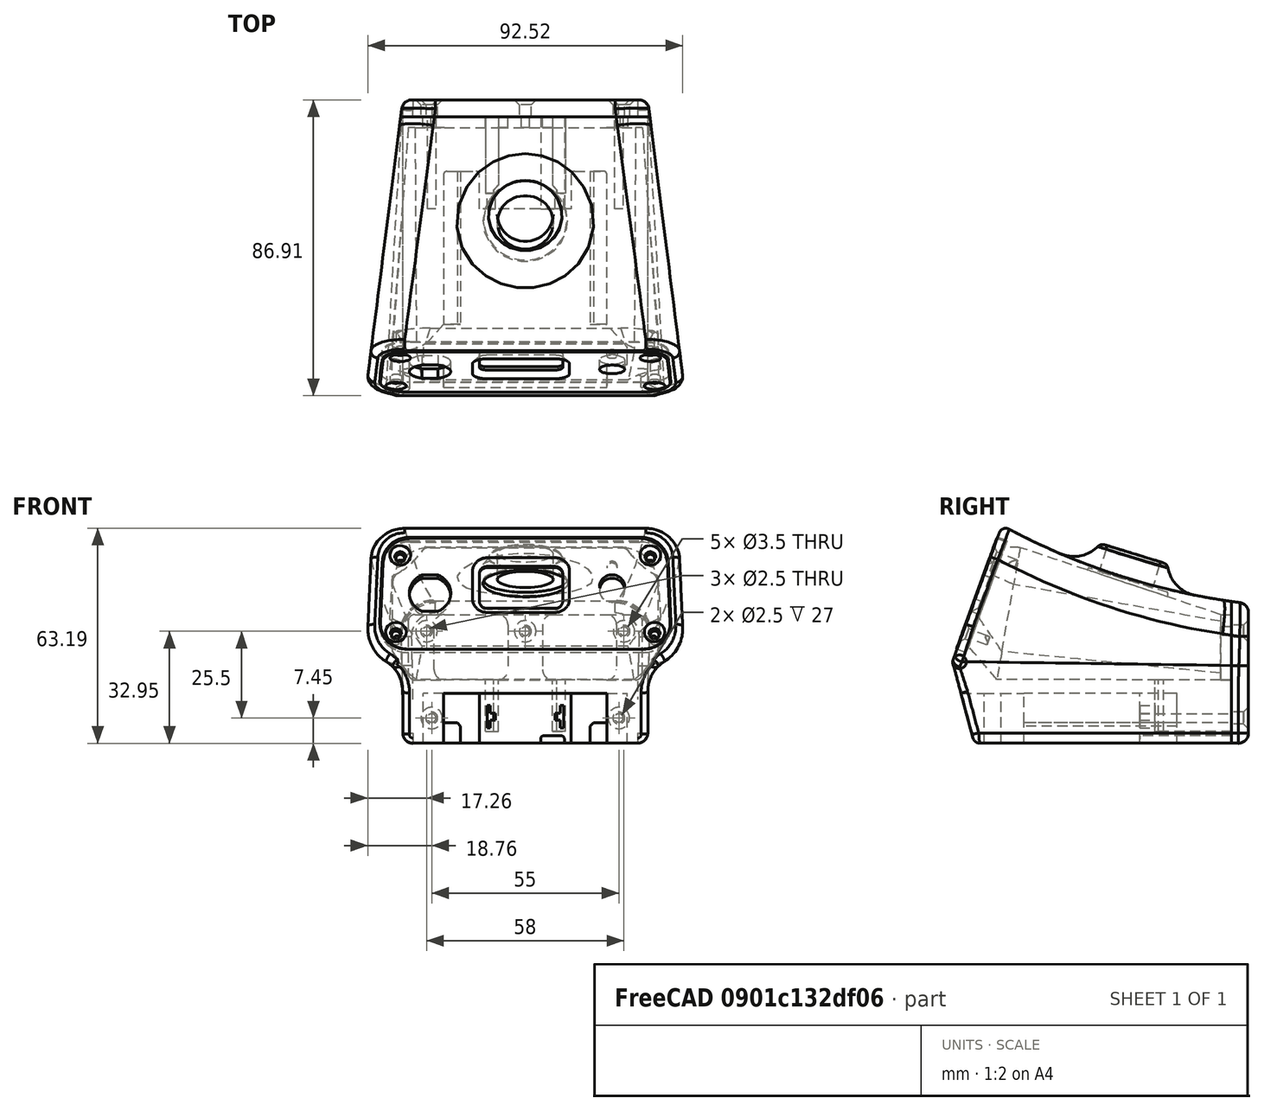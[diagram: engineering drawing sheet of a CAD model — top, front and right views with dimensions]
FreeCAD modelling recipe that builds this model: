
FCSTD DOCUMENT  (FreeCAD 2022.709R28846 (Git))
Label: solder_station4b_snap
License: All rights reserved
LicenseURL: http://en.wikipedia.org/wiki/All_rights_reserved
objects: Sketcher::SketchObject×20, PartDesign::Pocket×10, PartDesign::Fillet×8, Mesh::Feature×4, Part::FeaturePython×3, App::DocumentObjectGroup×3, PartDesign::Chamfer×3, PartDesign::Body×3, PartDesign::FeatureBase×2, PartDesign::Pad×2, Spreadsheet::Sheet×1, Part::Plane×1, Part::Loft×1, Part::Extrusion×1, Part::MultiCommon×1, PartDesign::SubtractiveLoft×1, PartDesign::Revolution×1, PartDesign::Groove×1, App::Part×1
note: 112 computed .brp shape members not serialized (recipe doc carries the construction recipe); baked Part::Feature solids carry a one-line shape summary decoded from their .brp

FEATURE [Sketcher::SketchObject] Sketch  label="RearSupport"
  ArcFitTolerance = 0
  AttachmentOffset = pos=(0,0,-37.8) rot=(0,0,1;0rad)
  AttachmentSupport = -> [XZ_Plane005]
  FullyConstrained = true
  MapMode = 5
  Placement = pos=(0,37.8,8.4e-15) rot=(1,0,0;1.5708rad)
  Support = -> [XZ_Plane005]
  TreeRank = 0
  expr: AttachmentOffset.Base.z = -<<param>>.mid_depth / 2 + <<param>>.wall
  expr: Constraints[24] = 3
  expr: Constraints[37] = <<param>>.bottom_height
  expr: Constraints[38] = <<param>>.floor
  expr: Constraints[39] = <<param>>.rear_height - <<param>>.wall
  expr: Constraints[47] = <<param>>.reart_screw_width2
  expr: Constraints[48] = <<param>>.rear_screw_width1
  expr: Constraints[49] = <<param>>.screw_hole
  expr: Constraints[50] = <<param>>.rear_screw_height
  expr: Constraints[51] = <<param>>.rear_screw_height
  expr: Constraints[52] = <<param>>.rear_screw_offset
  sketch-geometry (22):
    g0: LineSegment StartX=-23.8 StartY=13.8 StartZ=0 EndX=-8.1 EndY=13.8 EndZ=0
    g1: LineSegment StartX=26.8 StartY=10.8 StartZ=0 EndX=26.8 EndY=-2.4 EndZ=0
    g2: LineSegment StartX=23.8 StartY=-5.4 StartZ=0 EndX=8.1 EndY=-5.4 EndZ=0
    g3: LineSegment StartX=-26.8 StartY=-2.4 StartZ=0 EndX=-26.8 EndY=10.8 EndZ=0
    g4: LineSegment StartX=-5.1 StartY=10.8 StartZ=0 EndX=-5.1 EndY=-2.4 EndZ=0
    g5: LineSegment StartX=5.1 StartY=10.8 StartZ=0 EndX=5.1 EndY=-2.4 EndZ=0
    g6: LineSegment StartX=8.1 StartY=13.8 StartZ=0 EndX=23.8 EndY=13.8 EndZ=0
    g7: LineSegment StartX=-8.1 StartY=-5.4 StartZ=0 EndX=-23.8 EndY=-5.4 EndZ=0
    g8: ArcOfCircle CenterX=-8.1 CenterY=10.8 CenterZ=0 NormalX=0 NormalY=0 NormalZ=1 AngleXU=0 Radius=3 StartAngle=0 EndAngle=1.5708
    g9: ArcOfCircle CenterX=8.1 CenterY=10.8 CenterZ=0 NormalX=0 NormalY=0 NormalZ=1 AngleXU=0 Radius=3 StartAngle=1.5708 EndAngle=3.14159
    g10: ArcOfCircle CenterX=-8.1 CenterY=-2.4 CenterZ=0 NormalX=0 NormalY=0 NormalZ=1 AngleXU=0 Radius=3 StartAngle=4.71239 EndAngle=6.28319
    g11: ArcOfCircle CenterX=8.1 CenterY=-2.4 CenterZ=0 NormalX=0 NormalY=0 NormalZ=1 AngleXU=0 Radius=3 StartAngle=3.14159 EndAngle=4.71239
    g12: ArcOfCircle CenterX=-23.8 CenterY=10.8 CenterZ=0 NormalX=0 NormalY=0 NormalZ=1 AngleXU=0 Radius=3 StartAngle=1.5708 EndAngle=3.14159
    g13: ArcOfCircle CenterX=-23.8 CenterY=-2.4 CenterZ=0 NormalX=0 NormalY=0 NormalZ=1 AngleXU=0 Radius=3 StartAngle=3.14159 EndAngle=4.71239
    g14: ArcOfCircle CenterX=23.8 CenterY=10.8 CenterZ=0 NormalX=0 NormalY=0 NormalZ=1 AngleXU=0 Radius=3 StartAngle=0 EndAngle=1.5708
    g15: ArcOfCircle CenterX=23.8 CenterY=-2.4 CenterZ=0 NormalX=0 NormalY=0 NormalZ=1 AngleXU=0 Radius=3 StartAngle=4.71239 EndAngle=6.28319
    g16: Circle [constr] CenterX=0 CenterY=-24 CenterZ=0 NormalX=0 NormalY=0 NormalZ=1 AngleXU=0 Radius=3
    g17: Circle CenterX=0 CenterY=8.9 CenterZ=0 NormalX=0 NormalY=0 NormalZ=1 AngleXU=0 Radius=1.25
    g18: Circle CenterX=-29 CenterY=8.9 CenterZ=0 NormalX=0 NormalY=0 NormalZ=1 AngleXU=0 Radius=1.25
    g19: Circle [constr] CenterX=-27.5 CenterY=-16.6 CenterZ=0 NormalX=0 NormalY=0 NormalZ=1 AngleXU=0 Radius=1.25
    g20: Circle [constr] CenterX=27.5 CenterY=-16.6 CenterZ=0 NormalX=0 NormalY=0 NormalZ=1 AngleXU=0 Radius=1.25
    g21: Circle CenterX=29 CenterY=8.9 CenterZ=0 NormalX=0 NormalY=0 NormalZ=1 AngleXU=0 Radius=1.25
  constraints (53):
    c: Horizontal(g0)
    c: Horizontal(g2)
    c: Vertical(g1)
    c: Vertical(g3)
    c: Vertical(g4)
    c: Vertical(g5)
    c: Tangent(g0,g6)
    c: Tangent(g2,g7)
    c: Tangent(g0,g8) = 1.5708
    c: Tangent(g4,g8) = 1.5708
    c: Tangent(g5,g9) = -1.5708
    c: Tangent(g6,g9) = 1.5708
    c: Tangent(g7,g10) = 1.5708
    c: Tangent(g4,g10) = 1.5708
    c: Tangent(g5,g11) = -1.5708
    c: Tangent(g2,g11) = 1.5708
    c: Tangent(g0,g12) = 1.5708
    c: Tangent(g3,g12) = 1.5708
    c: Tangent(g3,g13) = 1.5708
    c: Tangent(g7,g13) = 1.5708
    c: Tangent(g6,g14) = 1.5708
    c: Tangent(g1,g14) = 1.5708
    c: Tangent(g1,g15) = 1.5708
    c: Tangent(g2,g15) = 1.5708
    c: Radius(g9) = 3
    c: Equal(g12,g13)
    c: Equal(g13,g10)
    c: Equal(g10,g8)
    c: Equal(g11,g15)
    c: Equal(g15,g14)
    c: Equal(g14,g9)
    c: DistanceX(g4,g-1) = 5.1
    c: DistanceX(g5,g1) = 21.7
    c: Symmetric(g4,g5,g-2)
    c: Equal(g7,g2)
    c: PointOnObject(g16,g-2)
    c: Radius(g16) = 3
    c: DistanceY(g16,g-1) = 24
    c: DistanceY(g16,g2) = 18.6
    c: DistanceY(g16,g6) = 37.8
    c: PointOnObject(g17,g-2)
    c: Equal(g21,g18)
    c: Equal(g18,g19)
    c: Equal(g19,g20)
    c: Equal(g18,g17)
    c: Symmetric(g20,g19,g-2)
    c: Symmetric(g18,g21,g-2)
    c: DistanceX(g19,g20) = 55
    c: DistanceX(g18,g21) = 58
    c: Diameter(g19) = 2.5
    c: DistanceY(g20,g21) = 25.5
    c: DistanceY(g20,g17) = 25.5
    c: DistanceY(g16,g19) = 7.4
FEATURE [Spreadsheet::Sheet] Spreadsheet  label="param"
  PythonMode = false
  ShowCells = 0
  TreeRank = 0
  cells = A1=Body; B2=top_depth; C2(top_depth)=70; B3=mid_depth; C3(mid_depth)=82; D3=Half value is the rear reference point; B4=bottom_depth; C4(bottom_depth)=75; B6=bottom_width; C6(bottom_width)=72; B7=bottom_height; C7(bottom_height)=24; B8=bottom_angle; C8(bottom_angle)=15; B10=rear_width; C10(rear_width)=72; B11=rear_height; C11(rear_height)=41; B13=mid_width; C13(mid_width)=80; B14=mid_height; C14(mid_height)=52; D14=was 50; B16=front_width1; C16(front_width1)=91; D16=@top (upper); B17=front_width2; C17(front_width2)=94; D17=@mid (lower); B18=front_height; C18(front_height)=64; B19=front_angle; C19(front_angle)=20; D19=20 is actual value; B21=wall; C21(wall)=3.2; B22=radius_big; C22(radius_big)=10; B23=radius_medium; C23(radius_medium)=3; B24=radius_small; C24(radius_small)=2; B25=arch; C25(arch)=200; A27=Button; B28=button_offset; C28(button_offset)=10; B29=button_inside_dia; C29(button_inside_dia)=20; B30=button_outside_dia; C30(button_outside_dia)=22; B31=button_height; C31(button_height)=24; B32=button_extension; C32(button_extension)=8; B33=button_fillet; C33(button_fillet)=12; B34=button_angle; C34(button_angle)=-17; B35=button_hole; C35(button_hole)=16.4; B36=button_hole_center; C36(button_hole_center)=-0.5; A38=Battery Cuts; B39=batt_carveout; C39(batt_carveout)=14.6; B40=batt_rail; C40(batt_rail)=6; B41=batt_rail_length; C41(batt_rail_length)=45; A43=Terminal Pockets; B44=terminal_height; C44(terminal_height)=6.6; B45=terminal_thickness; C45(terminal_thickness)=1; B46=terminal_seperation; C46(terminal_seperation)=21.5; B47=terminal_offset; C47(terminal_offset)=4.5; B48=terminal_depth; C48(terminal_depth)=22.5; A50=Box Interior; B51=floor; C51(floor)=18.6; B52=rear_inside_width; C52(rear_inside_width)==C10 - C21; D52=Calculated; B53=rear_inside_height; C53(rear_inside_height)==C11 - C21; D53=Calculated; B54=mid_inside_width; C54(mid_inside_width)==C13; D54=Calculated; B55=mid_inside_height; C55(mid_inside_height)==C14 + 6; D55=Calculated; B56=front_inside_width1; C56(front_inside_width1)==C63 - C59 * 2; D56=Calculated (upper); B57=front_inside_width2; C57(front_inside_width2)==C64 - C59 * 2; D57=Calculated (lower); B58=front_inside_height; C58(front_inside_height)==C65 - C60 * 2; D58=Calculated; B59=front_width_lip_width; C59(front_width_lip_width)=3; B60=front_inside_lip_height; C60(front_inside_lip_height)=2; A62=Face; B63=face_width1; C63(face_width1)=84; D63=Dimension of opening in case (upper); B64=face_width2; C64(face_width2)=85.5; D64=Dimension of opening in case (lower); B65=face_height; C65(face_height)==34 + 1; D65=Dimension of actual opening in case; B66=face_fit; C66(face_fit)=0.4; D66=Reduction of face dimensions for clearance with case; B67=face_thickness; C67(face_thickness)=3; D67=Face thickness; B68=face_radius; C68(face_radius)=8; D68=Corner radius; B69=face_offset; C69(face_offset)=2.8; D69=Axis origin to bottom face (reference); B70=face_knob_x; C70(face_knob_x)=25.5; D70=Vertical center line of face to center of knob; B71=face_knob_y; C71(face_knob_y)=19.5; D71=Bottom of face to center of knob; E71=was 20.5; B72=face_knob_tab; C72(face_knob_tab)=7; D72=Center to center distance of rotary dial shaft to tab; B73=face_knob_hole; C73(face_knob_hole)=7.4; D73=Hole size fo shaft; B74=face_screen_x; C74(face_screen_x)=14.5; D74=Center of knob to right edge of screen; B75=face_screen_y; C75(face_screen_y)=20; D75=Bottom of face to center of screen; E75=was 21; B76=face_screen_width; C76(face_screen_width)=24.5; D76=Width of screen opening; B77=face_screen_height; C77(face_screen_height)=13.1; D77=Height of screen opening; B78=face_screen_radius; C78(face_screen_radius)=2.25; D78=Radius of screen opening; B79=face_plug_x; C79(face_plug_x)=28; D79=Center line of face to center of plug; B80=face_plug_y; C80(face_plug_y)=17.5; D80=Bottom of face to center of plug; B81=face_plug_hole; C81(face_plug_hole)=12.2; D81=Hole size for plug body; A83=Screws; B84=screw_hole; C84(screw_hole)=2.5; D84=Screw hole diameter; B86=front_screw_width1; C86(front_screw_width1)=73.5; D86=Screw center to center distance (upper); B87=front_screw_width2; C87(front_screw_width2)=76; D87=Screw center to center distance (lower); B88=front_screw_height; C88(front_screw_height)=24; D88=Screw center to center distance (top to bottom); B89=front_screw_offset; C89(front_screw_offset)=5.5; D89=Bottom of face to center of screws (lower); B91=rear_screw_width1; C91(rear_screw_width1)=58; D91=Screw center to center distance (upper); B92=reart_screw_width2; C92(reart_screw_width2)=55; D92=Screw center to center distance (lower); B93=rear_screw_height; C93(rear_screw_height)=25.5; D93=Screw center to center distance (top to bottom); B94=rear_screw_offset; C94(rear_screw_offset)=7.4; A96=Back; B97=back_thickness; C97(back_thickness)=5
FEATURE [Sketcher::SketchObject] Sketch008  label="SketchButtonHole"
  ArcFitTolerance = 0
  AttachmentOffset = pos=(0,-0.5,24) rot=(1,0,0;-0.296706rad)
  AttachmentSupport = -> [XY_Plane005]
  FullyConstrained = true
  MapMode = 5
  Placement = pos=(0,-0.5,24) rot=(1,0,0;5.98648rad)
  Support = -> [XY_Plane005]
  TreeRank = 0
  expr: AttachmentOffset.Base.y = <<param>>.button_hole_center
  expr: AttachmentOffset.Base.z = <<param>>.button_height
  expr: AttachmentOffset.Rotation.Angle = <<param>>.button_angle
  expr: Constraints[0] = <<param>>.button_hole
  expr: Constraints[2] = <<param>>.button_offset
  sketch-geometry (1):
    g0: Circle CenterX=0 CenterY=10 CenterZ=0 NormalX=0 NormalY=0 NormalZ=1 AngleXU=0 Radius=8.2
  constraints (3):
    c: Diameter(g0) = 16.4
    c: PointOnObject(g0,g-2)
    c: DistanceY(g-1,g0) = 10
FEATURE [Sketcher::SketchObject] Sketch012  label="SketchSide"
  ArcFitTolerance = 0
  AttachmentOffset = pos=(2.5,0,0) rot=(0,0,1;0rad)
  AttachmentSupport = -> [YZ_Plane006]
  FullyConstrained = true
  MapMode = 5
  Placement = pos=(6e-16,2.5,-6e-16) rot=(0.57735,0.57735,0.57735;2.0944rad)
  Support = -> [YZ_Plane006]
  TreeRank = 0
  expr: AttachmentOffset.Base.x = <<param>>.back_thickness / 2
  expr: Constraints[10] = <<param>>.bottom_height
  expr: Constraints[11] = 90 - <<param>>.bottom_angle
  expr: Constraints[12] = 90 - <<param>>.front_angle
  expr: Constraints[16] = <<param>>.front_height
  expr: Constraints[4] = <<param>>.rear_height - <<param>>.bottom_height
  expr: Constraints[5] = <<param>>.arch
  expr: Constraints[6] = <<param>>.mid_depth + <<param>>.back_thickness
  sketch-geometry (6):
    g0: LineSegment StartX=43.5 StartY=0 StartZ=0 EndX=43.5 EndY=17 EndZ=0
    g1: LineSegment StartX=-43.5 StartY=0 StartZ=0 EndX=-28.9412 EndY=40 EndZ=0
    g2: ArcOfCircle CenterX=66.6993 CenterY=215.65 CenterZ=0 NormalX=0 NormalY=0 NormalZ=1 AngleXU=0 Radius=200 StartAngle=4.21378 EndAngle=4.59613
    g3: LineSegment StartX=-43.5 StartY=0 StartZ=0 EndX=-37.0692 EndY=-24 EndZ=0
    g4: LineSegment StartX=-37.0692 StartY=-24 StartZ=0 EndX=43.5 EndY=-24 EndZ=0
    g5: LineSegment StartX=43.5 StartY=-24 StartZ=0 EndX=43.5 EndY=0 EndZ=0
  constraints (18):
    c: PointOnObject(g1,g-1)
    c: Vertical(g0)
    c: Coincident(g2,g0)
    c: Symmetric(g1,g0,g-2)
    c: DistanceY(g0,g0) = 17
    c: Radius(g2) = 200
    c: DistanceX(g1,g0) = 87
    c: Horizontal(g4)
    c: Coincident(g5,g4)
    c: Vertical(g5)
    c: DistanceY(g4,g-1) = 24
    c: Angle(g3,g-1) = 1.309
    c: Angle(g-1,g1) = 1.22173
    c: Coincident(g3,g1)
    c: Coincident(g5,g0)
    c: Coincident(g2,g1)
    c: DistanceY(g4,g1) = 64
    c: Coincident(g4,g3)
FEATURE [Sketcher::SketchObject] Sketch018  label="SketchBat1"
  ArcFitTolerance = 0
  AttachmentOffset = pos=(0,0,-24) rot=(0,0,1;0rad)
  AttachmentSupport = -> [XY_Plane005]
  FullyConstrained = true
  MapMode = 5
  Placement = pos=(0,0,-24) rot=(0,0,1;0rad)
  Support = -> [XY_Plane005]
  TreeRank = 0
  expr: AttachmentOffset.Base.z = -<<param>>.bottom_height
  expr: Constraints[63] = <<param>>.batt_rail_length
  expr: Constraints[64] = <<param>>.mid_depth / 2
  sketch-geometry (21):
    g0: LineSegment StartX=-24 StartY=-41.7082 StartZ=0 EndX=24 EndY=-41.7082 EndZ=0
    g1: LineSegment StartX=24 StartY=-41.7082 StartZ=0 EndX=24 EndY=-31.7082 EndZ=0
    g2: LineSegment StartX=24 StartY=-31.7082 StartZ=0 EndX=30 EndY=-31.7082 EndZ=0
    g3: LineSegment StartX=30 StartY=-31.7082 StartZ=0 EndX=30 EndY=-26.7082 EndZ=0
    g4: LineSegment StartX=30 StartY=-26.7082 StartZ=0 EndX=24 EndY=-20 EndZ=0
    g5: LineSegment StartX=24 StartY=-20 StartZ=0 EndX=24 EndY=24 EndZ=0
    g6: LineSegment StartX=13.5 StartY=24 StartZ=0 EndX=13.5 EndY=14 EndZ=0
    g7: LineSegment StartX=13.5 StartY=14 StartZ=0 EndX=-13.5 EndY=14 EndZ=0
    g8: LineSegment StartX=-13.5 StartY=14 StartZ=0 EndX=-13.5 EndY=24 EndZ=0
    g9: LineSegment StartX=-24 StartY=24 StartZ=0 EndX=-24 EndY=-20 EndZ=0
    g10: LineSegment StartX=-24 StartY=-20 StartZ=0 EndX=-30 EndY=-26.7082 EndZ=0
    g11: LineSegment StartX=-30 StartY=-26.7082 StartZ=0 EndX=-30 EndY=-31.7082 EndZ=0
    g12: LineSegment StartX=-30 StartY=-31.7082 StartZ=0 EndX=-24 EndY=-31.7082 EndZ=0
    g13: LineSegment StartX=-24 StartY=-31.7082 StartZ=0 EndX=-24 EndY=-41.7082 EndZ=0
    g14: Circle [constr] CenterX=0 CenterY=41 CenterZ=0 NormalX=0 NormalY=0 NormalZ=1 AngleXU=0 Radius=4
    g15: ArcOfCircle CenterX=-14.5 CenterY=24 CenterZ=0 NormalX=0 NormalY=0 NormalZ=1 AngleXU=0 Radius=1 StartAngle=6.28318 EndAngle=7.85399
    g16: LineSegment StartX=-23 StartY=25 StartZ=0 EndX=-14.5 EndY=25 EndZ=0
    g17: LineSegment StartX=14.5 StartY=25 StartZ=0 EndX=23 EndY=25 EndZ=0
    g18: ArcOfCircle CenterX=-23 CenterY=24 CenterZ=0 NormalX=0 NormalY=0 NormalZ=1 AngleXU=0 Radius=1 StartAngle=1.57079 EndAngle=3.1416
    g19: ArcOfCircle CenterX=14.5 CenterY=24 CenterZ=0 NormalX=0 NormalY=0 NormalZ=1 AngleXU=0 Radius=1 StartAngle=1.5708 EndAngle=3.14159
    g20: ArcOfCircle CenterX=23 CenterY=24 CenterZ=0 NormalX=0 NormalY=0 NormalZ=1 AngleXU=0 Radius=1.00001 StartAngle=2.75124e-06 EndAngle=1.5708
  constraints (65):
    c: Horizontal(g0)
    c: Coincident(g1,g0)
    c: Vertical(g1)
    c: Coincident(g2,g1)
    c: Horizontal(g2)
    c: Coincident(g3,g2)
    c: Coincident(g3,g4)
    c: Vertical(g5)
    c: Coincident(g6,g7)
    c: Coincident(g7,g8)
    c: Vertical(g8)
    c: Vertical(g9)
    c: Coincident(g10,g11)
    c: Vertical(g11)
    c: Coincident(g11,g12)
    c: Horizontal(g12)
    c: Coincident(g12,g13)
    c: Equal(g6,g8)
    c: Equal(g5,g9)
    c: Equal(g4,g10)
    c: Equal(g3,g11)
    c: Equal(g12,g2)
    c: Equal(g1,g13)
    c: Coincident(g13,g0)
    c: Vertical(g13)
    c: DistanceX(g7,g7) = 27
    c: Symmetric(g7,g6,g-2)
    c: Distance(g4) = 9
    c: Vertical(g3)
    c: DistanceY(g3,g3) = 5
    c: DistanceX(g2,g2) = 6
    c: DistanceY(g1,g1) = 10
    c: DistanceX(g0,g0) = 48
    c: PointOnObject(g14,g-2)
    c: Coincident(g9,g10)
    c: Coincident(g5,g4)
    c: Coincident(g15,g8)
    c: Coincident(g16,g15)
    c: Tangent(g15,g8)
    c: Horizontal(g16)
    c: Horizontal(g17)
    c: DistanceX(g9,g5) = 48
    c: Symmetric(g4,g9,g-2)
    c: Equal(g16,g17)
    c: Coincident(g18,g9)
    c: Coincident(g18,g16)
    c: Equal(g18,g15)
    c: Tangent(g18,g16)
    c: Tangent(g18,g9)
    c: DistanceY(g6,g17) = 11
    c: Vertical(g6)
    c: Coincident(g19,g6)
    c: Coincident(g19,g17)
    c: Coincident(g20,g17)
    c: Coincident(g20,g5)
    c: Tangent(g20,g17)
    c: Tangent(g20,g5)
    c: Tangent(g19,g6)
    c: Tangent(g19,g17)
    c: Equal(g15,g19)
    c: Radius(g19) = 1
    c: Radius(g14) = 4
    c: DistanceY(g15,g14) = 16
    c: DistanceY(g9,g16) = 45
    c: DistanceY(g-1,g14) = 41
FEATURE [Sketcher::SketchObject] Sketch019  label="SketchBat2"
  ArcFitTolerance = 0
  AttachmentOffset = pos=(0,0,-25) rot=(0,0,1;0rad)
  AttachmentSupport = -> [XZ_Plane005]
  FullyConstrained = true
  MapMode = 5
  Placement = pos=(0,25,5.6e-15) rot=(1,0,0;1.5708rad)
  Support = -> [XZ_Plane005]
  TreeRank = 0
  expr: AttachmentOffset.Base.z = -<<param>>.mid_depth / 2 + 16
  expr: Constraints[17] = <<param>>.bottom_height
  expr: Constraints[18] = <<param>>.batt_rail
  expr: Constraints[19] = 48.01mm
  sketch-geometry (10):
    g0: LineSegment StartX=-24.005 StartY=-18 StartZ=0 EndX=-20.005 EndY=-18 EndZ=0
    g1: LineSegment StartX=-19.005 StartY=-24 StartZ=0 EndX=-24.005 EndY=-24 EndZ=0
    g2: LineSegment StartX=-24.005 StartY=-24 StartZ=0 EndX=-24.005 EndY=-18 EndZ=0
    g3: LineSegment StartX=24.005 StartY=-18 StartZ=0 EndX=20.005 EndY=-18 EndZ=0
    g4: LineSegment StartX=19.005 StartY=-24 StartZ=0 EndX=24.005 EndY=-24 EndZ=0
    g5: LineSegment StartX=24.005 StartY=-24 StartZ=0 EndX=24.005 EndY=-18 EndZ=0
    g6: LineSegment StartX=-19.005 StartY=-19 StartZ=0 EndX=-19.005 EndY=-24 EndZ=0
    g7: LineSegment StartX=19.005 StartY=-24 StartZ=0 EndX=19.005 EndY=-19 EndZ=0
    g8: LineSegment StartX=-20.005 StartY=-18 StartZ=0 EndX=-19.005 EndY=-19 EndZ=0
    g9: LineSegment StartX=19.005 StartY=-19 StartZ=0 EndX=20.005 EndY=-18 EndZ=0
  constraints (29):
    c: Coincident(g1,g2)
    c: Coincident(g2,g0)
    c: Horizontal(g0)
    c: Horizontal(g1)
    c: Vertical(g2)
    c: Coincident(g4,g5)
    c: Coincident(g5,g3)
    c: Horizontal(g3)
    c: Horizontal(g4)
    c: Vertical(g5)
    c: Coincident(g6,g1)
    c: Vertical(g6)
    c: Equal(g1,g4)
    c: Coincident(g7,g4)
    c: Vertical(g7)
    c: Equal(g6,g7)
    c: Symmetric(g1,g4,g-2)
    c: DistanceY(g1,g-1) = 24
    c: DistanceY(g4,g3) = 6
    c: DistanceX(g1,g4) = 48.01
    c: DistanceX(g4,g4) = 5
    c: Coincident(g8,g0)
    c: Coincident(g8,g6)
    c: Coincident(g9,g7)
    c: Coincident(g9,g3)
    c: Equal(g0,g3)
    c: Equal(g2,g5)
    c: DistanceX(g0,g0) = 4
    c: DistanceY(g1,g6) = 5
FEATURE [Sketcher::SketchObject] Sketch021  label="SketchButton"
  ArcFitTolerance = 0
  AttachmentOffset = pos=(10,24,0) rot=(0,0,1;-0.296706rad)
  AttachmentSupport = -> [YZ_Plane005]
  FullyConstrained = true
  MapMode = 5
  Placement = pos=(-3.1e-15,10,24) rot=(-0.51122,-0.690875,-0.51122;4.35074rad)
  Support = -> [YZ_Plane005]
  TreeRank = 0
  expr: AttachmentOffset.Base.x = <<param>>.button_offset
  expr: AttachmentOffset.Base.y = <<param>>.button_height
  expr: AttachmentOffset.Rotation.Angle = <<param>>.button_angle
  expr: Constraints[6] = <<param>>.button_extension
  expr: Constraints[7] = <<param>>.button_outside_dia / 2
  sketch-geometry (5):
    g0: LineSegment StartX=0 StartY=0 StartZ=0 EndX=0 EndY=8 EndZ=0
    g1: LineSegment StartX=0 StartY=8 StartZ=0 EndX=9 EndY=8 EndZ=0
    g2: LineSegment StartX=0 StartY=0 StartZ=0 EndX=11 EndY=0 EndZ=0
    g3: LineSegment StartX=11 StartY=0 StartZ=0 EndX=11 EndY=6 EndZ=0
    g4: ArcOfCircle CenterX=9 CenterY=6 CenterZ=0 NormalX=0 NormalY=0 NormalZ=1 AngleXU=0 Radius=2 StartAngle=1.123e-13 EndAngle=1.5708
  constraints (13):
    c: Coincident(g0,g-1)
    c: PointOnObject(g0,g-2)
    c: Coincident(g1,g0)
    c: Horizontal(g1)
    c: Coincident(g2,g0)
    c: Horizontal(g2)
    c: DistanceY(g0,g0) = 8
    c: DistanceX(g2,g2) = 11
    c: Coincident(g3,g2)
    c: Vertical(g3)
    c: Radius(g4) = 2
    c: Tangent(g4,g3) = -1.5708
    c: Tangent(g4,g1) = 1.5708
FEATURE [Sketcher::SketchObject] Sketch022  label="SketchRearInside"
  ArcFitTolerance = 0
  AttachmentOffset = pos=(0,0,-37.8) rot=(0,0,1;0rad)
  AttachmentSupport = -> [XZ_Plane005]
  FullyConstrained = true
  MapMode = 5
  Placement = pos=(0,37.8,8.4e-15) rot=(1,0,0;1.5708rad)
  Support = -> [XZ_Plane005]
  TreeRank = 0
  expr: AttachmentOffset.Base.z = -<<param>>.mid_depth / 2 + <<param>>.wall
  expr: Constraints[12] = <<param>>.radius_small
  expr: Constraints[18] = <<param>>.rear_inside_width
  expr: Constraints[26] = <<param>>.bottom_height
  expr: Constraints[27] = <<param>>.rear_inside_height
  expr: Constraints[29] = <<param>>.floor
  sketch-geometry (9):
    g0: LineSegment StartX=-34.4 StartY=11.8 StartZ=0 EndX=-34.4 EndY=-3.39998 EndZ=0
    g1: LineSegment StartX=-32.4 StartY=-5.4 StartZ=0 EndX=32.4 EndY=-5.4 EndZ=0
    g2: LineSegment StartX=34.4 StartY=-3.39998 StartZ=0 EndX=34.4 EndY=11.8 EndZ=0
    g3: LineSegment StartX=-32.4 StartY=13.8 StartZ=0 EndX=32.4 EndY=13.8 EndZ=0
    g4: ArcOfCircle CenterX=32.4 CenterY=11.8 CenterZ=0 NormalX=0 NormalY=0 NormalZ=1 AngleXU=0 Radius=2 StartAngle=6.28318 EndAngle=7.85399
    g5: ArcOfCircle CenterX=32.4 CenterY=-3.4 CenterZ=0 NormalX=0 NormalY=0 NormalZ=1 AngleXU=0 Radius=2 StartAngle=4.71238 EndAngle=6.28319
    g6: ArcOfCircle CenterX=-32.4 CenterY=11.8 CenterZ=0 NormalX=0 NormalY=0 NormalZ=1 AngleXU=0 Radius=2 StartAngle=1.57079 EndAngle=3.1416
    g7: ArcOfCircle CenterX=-32.4 CenterY=-3.4 CenterZ=0 NormalX=0 NormalY=0 NormalZ=1 AngleXU=0 Radius=2 StartAngle=3.14158 EndAngle=4.71239
    g8: Circle [constr] CenterX=0 CenterY=-24 CenterZ=0 NormalX=0 NormalY=0 NormalZ=1 AngleXU=0 Radius=3
  constraints (30):
    c: Vertical(g0)
    c: Horizontal(g1)
    c: Vertical(g2)
    c: Horizontal(g3)
    c: Equal(g3,g1)
    c: Equal(g0,g2)
    c: Coincident(g4,g3)
    c: Coincident(g4,g2)
    c: Coincident(g5,g2)
    c: Coincident(g5,g1)
    c: Coincident(g6,g0)
    c: Coincident(g6,g3)
    c: Radius(g6) = 2
    c: Equal(g6,g4)
    c: Equal(g4,g5)
    c: Coincident(g7,g1)
    c: Coincident(g7,g0)
    c: Equal(g5,g7)
    c: DistanceX(g0,g2) = 68.8
    c: Symmetric(g0,g2,g-2)
    c: Tangent(g4,g2)
    c: Tangent(g4,g3)
    c: Tangent(g5,g2)
    c: Tangent(g5,g1)
    c: Tangent(g6,g3)
    c: PointOnObject(g8,g-2)
    c: DistanceY(g8,g-1) = 24
    c: DistanceY(g8,g3) = 37.8
    c: Radius(g8) = 3
    c: DistanceY(g8,g1) = 18.6
FEATURE [Sketcher::SketchObject] Sketch023  label="SketchFrontInside"
  ArcFitTolerance = 0
  AttachmentOffset = pos=(0,0,38) rot=(1,0,0;-0.349066rad)
  AttachmentSupport = -> [XZ_Plane005]
  FullyConstrained = true
  MapMode = 5
  Placement = pos=(0,-38,-8.4e-15) rot=(-1,0,0;5.06145rad)
  Support = -> [XZ_Plane005]
  TreeRank = 0
  expr: AttachmentOffset.Base.z = <<param>>.mid_depth / 2 - <<param>>.face_thickness
  expr: AttachmentOffset.Rotation.Angle = -<<param>>.front_angle
  expr: Constraints[1] = <<param>>.front_inside_width1
  expr: Constraints[23] = <<param>>.front_inside_height / 2 - 13 / 2
  expr: Constraints[24] = 59 + 1.5
  expr: Constraints[2] = <<param>>.front_inside_height
  expr: Constraints[7] = <<param>>.front_inside_width2
  expr: Constraints[8] = <<param>>.front_inside_width2 / 2
  expr: Constraints[9] = <<param>>.face_offset + <<param>>.front_inside_lip_height
  sketch-geometry (8):
    g0: LineSegment StartX=-30.25 StartY=4.8 StartZ=0 EndX=30.25 EndY=4.8 EndZ=0
    g1: LineSegment StartX=29.5 StartY=35.8 StartZ=0 EndX=-29.5 EndY=35.8 EndZ=0
    g2: LineSegment StartX=-39 StartY=26.8 StartZ=0 EndX=-39.75 EndY=13.8 EndZ=0
    g3: LineSegment StartX=39 StartY=26.8 StartZ=0 EndX=39.75 EndY=13.8 EndZ=0
    g4: ArcOfCircle CenterX=-48.6957 CenterY=46.5482 CenterZ=0 NormalX=0 NormalY=0 NormalZ=1 AngleXU=0 Radius=22 StartAngle=5.16878 EndAngle=5.77275
    g5: ArcOfCircle CenterX=48.6957 CenterY=46.5482 CenterZ=0 NormalX=0 NormalY=0 NormalZ=1 AngleXU=0 Radius=22 StartAngle=3.65203 EndAngle=4.256
    g6: ArcOfCircle CenterX=49.4457 CenterY=-5.94825 CenterZ=0 NormalX=0 NormalY=0 NormalZ=1 AngleXU=0 Radius=22 StartAngle=2.02719 EndAngle=2.63116
    g7: ArcOfCircle CenterX=-49.4457 CenterY=-5.94825 CenterZ=0 NormalX=0 NormalY=0 NormalZ=1 AngleXU=0 Radius=22 StartAngle=0.510435 EndAngle=1.1144
  constraints (25):
    c: Symmetric(g0,g0,g-2)
    c: DistanceX(g2,g3) = 78
    c: DistanceY(g0,g1) = 31
    c: Symmetric(g1,g1,g-2)
    c: DistanceY(g3,g3) = 13
    c: Equal(g3,g2)
    c: DistanceX(g1,g1) = 59
    c: DistanceX(g2,g3) = 79.5
    c: DistanceX(g2,g-1) = 39.75
    c: DistanceY(g-1,g0) = 4.8
    c: Coincident(g4,g2)
    c: Coincident(g4,g1)
    c: Coincident(g5,g1)
    c: Coincident(g5,g3)
    c: Coincident(g6,g3)
    c: Coincident(g6,g0)
    c: Coincident(g7,g2)
    c: Coincident(g7,g0)
    c: Equal(g5,g4)
    c: Equal(g4,g7)
    c: Equal(g7,g6)
    c: Radius(g5) = 22
    c: Symmetric(g3,g2,g-2)
    c: DistanceY(g0,g3) = 9
    c: Distance(g0) = 60.5
FEATURE [Sketcher::SketchObject] Sketch024  label="SketchFaceCut"
  ArcFitTolerance = 0
  AttachmentOffset = pos=(0,0,37.9) rot=(1,0,0;-0.349066rad)
  AttachmentSupport = -> [XZ_Plane005]
  FullyConstrained = true
  MapMode = 5
  Placement = pos=(0,-37.9,-8.4e-15) rot=(-1,0,0;5.06145rad)
  Support = -> [XZ_Plane005]
  TreeRank = 0
  expr: AttachmentOffset.Base.z = <<param>>.mid_depth / 2 - <<param>>.face_thickness - 0.1
  expr: AttachmentOffset.Rotation.Angle = -<<param>>.front_angle
  expr: Constraints[13] = <<param>>.face_radius
  expr: Constraints[22] = <<param>>.face_width1
  expr: Constraints[23] = <<param>>.face_width2
  expr: Constraints[24] = <<param>>.face_offset
  expr: Constraints[25] = <<param>>.face_height
  sketch-geometry (8):
    g0: LineSegment StartX=-34.0062 StartY=37.8 StartZ=0 EndX=34.0062 EndY=37.8 EndZ=0
    g1: LineSegment StartX=42 StartY=30.1155 StartZ=0 EndX=42.75 EndY=11.1155 EndZ=0
    g2: LineSegment StartX=34.7562 StartY=2.8 StartZ=0 EndX=-34.7562 EndY=2.8 EndZ=0
    g3: LineSegment StartX=-42.75 StartY=11.1155 StartZ=0 EndX=-42 EndY=30.1155 EndZ=0
    g4: ArcOfCircle CenterX=34.0062 CenterY=29.8 CenterZ=0 NormalX=0 NormalY=0 NormalZ=1 AngleXU=0 Radius=8 StartAngle=0.0394522 EndAngle=1.57079
    g5: ArcOfCircle CenterX=34.7562 CenterY=10.8 CenterZ=0 NormalX=0 NormalY=0 NormalZ=1 AngleXU=0 Radius=8 StartAngle=4.71239 EndAngle=6.32264
    g6: ArcOfCircle CenterX=-34.0062 CenterY=29.8 CenterZ=0 NormalX=0 NormalY=0 NormalZ=1 AngleXU=0 Radius=8 StartAngle=1.5708 EndAngle=3.10214
    g7: ArcOfCircle CenterX=-34.7562 CenterY=10.8 CenterZ=0 NormalX=0 NormalY=0 NormalZ=1 AngleXU=0 Radius=8 StartAngle=3.10214 EndAngle=4.71239
  constraints (27):
    c: Horizontal(g0)
    c: Coincident(g4,g0)
    c: Coincident(g4,g1)
    c: Coincident(g5,g1)
    c: Coincident(g5,g2)
    c: Coincident(g6,g0)
    c: Coincident(g6,g3)
    c: Coincident(g7,g3)
    c: Coincident(g7,g2)
    c: Equal(g1,g3)
    c: Equal(g4,g6)
    c: Equal(g6,g7)
    c: Equal(g7,g5)
    c: Radius(g4) = 8
    c: Tangent(g6,g3)
    c: Tangent(g7,g3)
    c: Tangent(g7,g2)
    c: Tangent(g6,g0)
    c: Tangent(g4,g0)
    c: Tangent(g4,g1)
    c: Tangent(g5,g1)
    c: Tangent(g5,g2)
    c: DistanceX(g3,g1) = 84
    c: DistanceX(g3,g1) = 85.5
    c: DistanceY(g-1,g2) = 2.8
    c: DistanceY(g2,g0) = 35
    c: Symmetric(g2,g2,g-2)
FEATURE [Sketcher::SketchObject] Sketch025  label="SketchMidInside"
  ArcFitTolerance = 0
  AttachmentOffset = pos=(0,0,27) rot=(1,0,0;-0.174533rad)
  AttachmentSupport = -> [XZ_Plane005]
  FullyConstrained = true
  MapMode = 5
  Placement = pos=(0,-27,-6e-15) rot=(-1,0,0;4.88692rad)
  Support = -> [XZ_Plane005]
  TreeRank = 0
  expr: AttachmentOffset.Base.z = <<param>>.mid_depth / 2 - 14
  expr: AttachmentOffset.Rotation.Angle = -<<param>>.front_angle / 2
  expr: Constraints[10] = <<param>>.radius_big + 1
  expr: Constraints[11] = <<param>>.floor
  expr: Constraints[12] = Spreadsheet.mid_inside_width - 2
  expr: Constraints[14] = <<param>>.mid_inside_height
  expr: Constraints[23] = <<param>>.mid_width - 16
  expr: Constraints[24] = 20mm
  expr: Constraints[4] = <<param>>.bottom_height
  sketch-geometry (9):
    g0: LineSegment StartX=-28 StartY=34 StartZ=0 EndX=28 EndY=34 EndZ=0
    g1: LineSegment StartX=39 StartY=23 StartZ=0 EndX=39 EndY=3 EndZ=0
    g2: LineSegment StartX=32 StartY=-5.4 StartZ=0 EndX=-32 EndY=-5.4 EndZ=0
    g3: LineSegment StartX=-39 StartY=3 StartZ=0 EndX=-39 EndY=23 EndZ=0
    g4: Circle [constr] CenterX=0 CenterY=-24 CenterZ=0 NormalX=0 NormalY=0 NormalZ=1 AngleXU=0 Radius=3
    g5: ArcOfCircle CenterX=-28 CenterY=23 CenterZ=0 NormalX=0 NormalY=0 NormalZ=1 AngleXU=0 Radius=11 StartAngle=1.5708 EndAngle=3.14159
    g6: ArcOfCircle CenterX=28 CenterY=23 CenterZ=0 NormalX=0 NormalY=0 NormalZ=1 AngleXU=0 Radius=11 StartAngle=0 EndAngle=1.5708
    g7: ArcOfCircle CenterX=-17.5474 CenterY=13.7605 CenterZ=0 NormalX=0 NormalY=0 NormalZ=1 AngleXU=0 Radius=24 StartAngle=3.60651 EndAngle=4.06615
    g8: ArcOfCircle CenterX=17.5474 CenterY=13.7605 CenterZ=0 NormalX=0 NormalY=0 NormalZ=1 AngleXU=0 Radius=24 StartAngle=5.35863 EndAngle=5.81826
  constraints (25):
    c: Vertical(g1)
    c: Vertical(g3)
    c: PointOnObject(g4,g-2)
    c: Radius(g4) = 3
    c: DistanceY(g4,g-1) = 24
    c: Tangent(g3,g5) = 1.5708
    c: Tangent(g0,g5) = 1.5708
    c: Tangent(g0,g6) = 1.5708
    c: Tangent(g1,g6) = 1.5708
    c: Equal(g6,g5)
    c: Radius(g6) = 11
    c: DistanceY(g4,g2) = 18.6
    c: DistanceX(g3,g1) = 78
    c: Symmetric(g2,g2,g-2)
    c: DistanceY(g4,g0) = 58
    c: Symmetric(g0,g0,g-2)
    c: Equal(g3,g1)
    c: Coincident(g7,g2)
    c: Coincident(g8,g1)
    c: Coincident(g8,g2)
    c: Coincident(g7,g3)
    c: Equal(g8,g7)
    c: Radius(g8) = 24
    c: DistanceX(g2,g2) = 64
    c: DistanceY(g1,g1) = 20
FEATURE [Sketcher::SketchObject] Sketch026  label="SketchFrontScrews"
  ArcFitTolerance = 0
  AttachmentOffset = pos=(0,0,38) rot=(1,0,0;-0.349066rad)
  AttachmentSupport = -> [XZ_Plane005]
  FullyConstrained = true
  MapMode = 5
  Placement = pos=(0,-38,-8.4e-15) rot=(-1,0,0;5.06145rad)
  Support = -> [XZ_Plane005]
  TreeRank = 0
  expr: AttachmentOffset.Base.z = <<param>>.mid_depth / 2 - <<param>>.face_thickness
  expr: AttachmentOffset.Rotation.Angle = -<<param>>.front_angle
  expr: Constraints[0] = <<param>>.front_screw_width1
  expr: Constraints[13] = <<param>>.screw_hole
  expr: Constraints[1] = <<param>>.front_screw_width2
  expr: Constraints[2] = <<param>>.front_screw_height
  expr: Constraints[9] = <<param>>.face_offset + <<param>>.front_screw_offset
  sketch-geometry (6):
    g0: Circle CenterX=-36.75 CenterY=32.3 CenterZ=0 NormalX=0 NormalY=0 NormalZ=1 AngleXU=0 Radius=1.25
    g1: Circle CenterX=36.75 CenterY=32.3 CenterZ=0 NormalX=0 NormalY=0 NormalZ=1 AngleXU=0 Radius=1.25
    g2: Circle CenterX=-38 CenterY=8.3 CenterZ=0 NormalX=0 NormalY=0 NormalZ=1 AngleXU=0 Radius=1.25
    g3: Circle CenterX=38 CenterY=8.3 CenterZ=0 NormalX=0 NormalY=0 NormalZ=1 AngleXU=0 Radius=1.25
    g4: LineSegment [constr] StartX=-36.75 StartY=32.3 StartZ=0 EndX=36.75 EndY=32.3 EndZ=0
    g5: LineSegment [constr] StartX=-38 StartY=8.3 StartZ=0 EndX=38 EndY=8.3 EndZ=0
  constraints (14):
    c: DistanceX(g0,g1) = 73.5
    c: DistanceX(g2,g3) = 76
    c: DistanceY(g3,g1) = 24
    c: Coincident(g4,g0)
    c: Coincident(g4,g1)
    c: Coincident(g5,g2)
    c: Coincident(g5,g3)
    c: Symmetric(g2,g3,g-2)
    c: Symmetric(g0,g1,g-2)
    c: DistanceY(g-1,g3) = 8.3
    c: Equal(g0,g2)
    c: Equal(g2,g3)
    c: Equal(g3,g1)
    c: Diameter(g0) = 2.5
FEATURE [Sketcher::SketchObject] Sketch027  label="SketchButtonCarve"
  ArcFitTolerance = 0
  AttachmentOffset = pos=(10,22,0) rot=(0,0,1;-0.296706rad)
  AttachmentSupport = -> [YZ_Plane005]
  FullyConstrained = true
  MapMode = 5
  Placement = pos=(-2.7e-15,10,22) rot=(-0.51122,-0.690875,-0.51122;4.35074rad)
  Support = -> [YZ_Plane005]
  TreeRank = 0
  expr: AttachmentOffset.Base.x = <<param>>.button_offset
  expr: AttachmentOffset.Base.y = <<param>>.button_height - 2
  expr: AttachmentOffset.Rotation.Angle = <<param>>.button_angle
  expr: Constraints[12] = <<param>>.button_hole / 2 + 10
  expr: Constraints[6] = <<param>>.button_hole / 2 + 4
  sketch-geometry (4):
    g0: LineSegment StartX=0 StartY=2 StartZ=0 EndX=12.2 EndY=2 EndZ=0
    g1: ArcOfCircle CenterX=18.2 CenterY=3.09999 CenterZ=0 NormalX=0 NormalY=0 NormalZ=1 AngleXU=0 Radius=6.09999 StartAngle=3.32291 EndAngle=4.71239
    g2: LineSegment StartX=0 StartY=2 StartZ=0 EndX=0 EndY=-3 EndZ=0
    g3: LineSegment StartX=18.2 StartY=-3 StartZ=0 EndX=0 EndY=-3 EndZ=0
  constraints (13):
    c: Horizontal(g0)
    c: Coincident(g1,g0)
    c: Coincident(g2,g0)
    c: Coincident(g3,g1)
    c: Horizontal(g3)
    c: Tangent(g3,g1)
    c: DistanceX(g0,g0) = 12.2
    c: DistanceY(g2,g2) = 5
    c: Coincident(g2,g3)
    c: Vertical(g2)
    c: PointOnObject(g-1,g2)
    c: DistanceY(g2,g-1) = 3
    c: DistanceX(g3,g3) = 18.2
FEATURE [Sketcher::SketchObject] Sketch028  label="SketchTerminals"
  ArcFitTolerance = 0
  AttachmentSupport = -> [XZ_Plane005]
  FullyConstrained = true
  MapMode = 5
  Placement = pos=(0,0,0) rot=(1,0,0;1.5708rad)
  Support = -> [XZ_Plane005]
  TreeRank = 0
  expr: Constraints[17] = <<param>>.terminal_thickness
  expr: Constraints[18] = <<param>>.terminal_height
  expr: Constraints[21] = <<param>>.bottom_height
  expr: Constraints[22] = <<param>>.terminal_offset
  expr: Constraints[23] = <<param>>.terminal_seperation
  sketch-geometry (17):
    g0: LineSegment StartX=10.25 StartY=-12.9 StartZ=0 EndX=11.25 EndY=-12.9 EndZ=0
    g1: LineSegment StartX=11.25 StartY=-12.9 StartZ=0 EndX=11.25 EndY=-19.5 EndZ=0
    g2: LineSegment StartX=11.25 StartY=-19.5 StartZ=0 EndX=10.25 EndY=-19.5 EndZ=0
    g3: LineSegment StartX=10.25 StartY=-19.5 StartZ=0 EndX=10.25 EndY=-17.25 EndZ=0
    g4: LineSegment StartX=-10.25 StartY=-12.9 StartZ=0 EndX=-11.25 EndY=-12.9 EndZ=0
    g5: LineSegment StartX=-11.25 StartY=-12.9 StartZ=0 EndX=-11.25 EndY=-19.5 EndZ=0
    g6: LineSegment StartX=-11.25 StartY=-19.5 StartZ=0 EndX=-10.25 EndY=-19.5 EndZ=0
    g7: LineSegment StartX=-10.25 StartY=-19.5 StartZ=0 EndX=-10.25 EndY=-17.25 EndZ=0
    g8: Circle [constr] CenterX=0 CenterY=-24 CenterZ=0 NormalX=0 NormalY=0 NormalZ=1 AngleXU=0 Radius=3
    g9: LineSegment StartX=-10.25 StartY=-15.15 StartZ=0 EndX=-8.75 EndY=-15.15 EndZ=0
    g10: LineSegment StartX=-10.25 StartY=-17.25 StartZ=0 EndX=-8.75 EndY=-17.25 EndZ=0
    g11: LineSegment StartX=-8.75 StartY=-15.15 StartZ=0 EndX=-8.75 EndY=-17.25 EndZ=0
    g12: LineSegment StartX=10.25 StartY=-15.15 StartZ=0 EndX=8.75 EndY=-15.15 EndZ=0
    g13: LineSegment StartX=8.75 StartY=-15.15 StartZ=0 EndX=8.75 EndY=-17.25 EndZ=0
    g14: LineSegment StartX=8.75 StartY=-17.25 StartZ=0 EndX=10.25 EndY=-17.25 EndZ=0
    g15: LineSegment StartX=-10.25 StartY=-15.15 StartZ=0 EndX=-10.25 EndY=-12.9 EndZ=0
    g16: LineSegment StartX=10.25 StartY=-15.15 StartZ=0 EndX=10.25 EndY=-12.9 EndZ=0
  constraints (48):
    c: Coincident(g0,g1)
    c: Coincident(g1,g2)
    c: Coincident(g2,g3)
    c: Coincident(g16,g0)
    c: Horizontal(g0)
    c: Horizontal(g2)
    c: Vertical(g1)
    c: Vertical(g3)
    c: Coincident(g4,g5)
    c: Coincident(g5,g6)
    c: Coincident(g6,g7)
    c: Coincident(g15,g4)
    c: Horizontal(g4)
    c: Horizontal(g6)
    c: Vertical(g5)
    c: Vertical(g7)
    c: Equal(g4,g0)
    c: DistanceX(g4,g4) = 1
    c: DistanceY(g3,g16) = 6.6
    c: PointOnObject(g8,g-2)
    c: Radius(g8) = 3
    c: DistanceY(g8,g-1) = 24
    c: DistanceY(g8,g1) = 4.5
    c: DistanceX(g6,g1) = 21.5
    c: Symmetric(g4,g0,g-2)
    c: Horizontal(g9)
    c: Horizontal(g10)
    c: Coincident(g11,g9)
    c: Coincident(g11,g10)
    c: Vertical(g11)
    c: Horizontal(g12)
    c: Coincident(g13,g12)
    c: Vertical(g13)
    c: Coincident(g14,g13)
    c: Horizontal(g14)
    c: Coincident(g7,g10)
    c: Coincident(g15,g9)
    c: Tangent(g7,g15)
    c: Coincident(g3,g14)
    c: Coincident(g16,g12)
    c: Tangent(g3,g16)
    c: Equal(g15,g7)
    c: Equal(g7,g3)
    c: Equal(g3,g16)
    c: Equal(g10,g14)
    c: Equal(g11,g13)
    c: DistanceY(g11,g11) = 2.1
    c: DistanceX(g12,g12) = 1.5
FEATURE [Sketcher::SketchObject] Sketch029  label="SketchAccess"
  ArcFitTolerance = 0
  AttachmentOffset = pos=(0,0,-20.5) rot=(0,0,1;0rad)
  AttachmentSupport = -> [XY_Plane005]
  FullyConstrained = true
  MapMode = 5
  Placement = pos=(0,0,-20.5) rot=(0,0,1;0rad)
  Support = -> [XY_Plane005]
  TreeRank = 0
  expr: AttachmentOffset.Base.z = -<<param>>.bottom_height + <<param>>.terminal_offset - 1
  expr: Constraints[20] = <<param>>.mid_depth / 2
  expr: Constraints[9] = <<param>>.terminal_seperation + <<param>>.terminal_thickness * 2
  sketch-geometry (12):
    g0: LineSegment StartX=-11.75 StartY=41 StartZ=0 EndX=-11.75 EndY=18.5 EndZ=0
    g1: LineSegment StartX=-7.95 StartY=41 StartZ=0 EndX=-7.95 EndY=21 EndZ=0
    g2: LineSegment StartX=7.95 StartY=41 StartZ=0 EndX=7.95 EndY=21 EndZ=0
    g3: LineSegment StartX=11.75 StartY=41 StartZ=0 EndX=11.75 EndY=18.5 EndZ=0
    g4: LineSegment StartX=-11.75 StartY=41 StartZ=0 EndX=-7.95 EndY=41 EndZ=0
    g5: LineSegment StartX=7.95 StartY=41 StartZ=0 EndX=11.75 EndY=41 EndZ=0
    g6: LineSegment StartX=-11.75 StartY=18.5 StartZ=0 EndX=-9.25 EndY=18.5 EndZ=0
    g7: LineSegment StartX=11.75 StartY=18.5 StartZ=0 EndX=9.25 EndY=18.5 EndZ=0
    g8: LineSegment StartX=-9.25 StartY=18.5 StartZ=0 EndX=-9.25 EndY=19.5 EndZ=0
    g9: LineSegment StartX=-9.25 StartY=19.5 StartZ=0 EndX=-7.95 EndY=21 EndZ=0
    g10: LineSegment StartX=9.25 StartY=18.5 StartZ=0 EndX=9.25 EndY=19.5 EndZ=0
    g11: LineSegment StartX=9.25 StartY=19.5 StartZ=0 EndX=7.95 EndY=21 EndZ=0
  constraints (35):
    c: Vertical(g0)
    c: Vertical(g2)
    c: Equal(g1,g2)
    c: Coincident(g4,g0)
    c: Coincident(g4,g1)
    c: Horizontal(g4)
    c: Coincident(g5,g2)
    c: Coincident(g5,g3)
    c: Horizontal(g5)
    c: DistanceX(g0,g3) = 23.5
    c: Vertical(g3)
    c: Equal(g5,g4)
    c: Symmetric(g1,g2,g-2)
    c: DistanceX(g4,g4) = 3.8
    c: Vertical(g1)
    c: Equal(g0,g3)
    c: Coincident(g6,g0)
    c: Horizontal(g6)
    c: Coincident(g7,g3)
    c: Equal(g6,g7)
    c: DistanceY(g-1,g3) = 41
    c: Horizontal(g7)
    c: Coincident(g8,g6)
    c: Vertical(g8)
    c: Coincident(g9,g8)
    c: Coincident(g9,g1)
    c: Coincident(g10,g7)
    c: Coincident(g11,g10)
    c: Coincident(g11,g2)
    c: Equal(g8,g10)
    c: Equal(g9,g11)
    c: DistanceY(g1,g1) = 20
    c: DistanceY(g0,g0) = 22.5
    c: DistanceX(g6,g6) = 2.5
    c: DistanceY(g8,g8) = 1
FEATURE [Sketcher::SketchObject] Sketch030  label="SketchFront"
  ArcFitTolerance = 0
  AttachmentOffset = pos=(0,0,41) rot=(0,0,1;0rad)
  AttachmentSupport = -> [XZ_Plane006]
  FullyConstrained = true
  MapMode = 5
  Placement = pos=(0,-41,-9.1e-15) rot=(1,0,0;1.5708rad)
  Support = -> [XZ_Plane006]
  TreeRank = 0
  expr: AttachmentOffset.Base.z = <<param>>.mid_depth / 2
  expr: Constraints[18] = <<param>>.radius_big * 1.2
  expr: Constraints[19] = <<param>>.radius_big
  expr: Constraints[2] = <<param>>.bottom_width
  expr: Constraints[4] = <<param>>.bottom_height + 10
  expr: Constraints[5] = <<param>>.front_width2
  expr: Constraints[6] = <<param>>.front_width2
  expr: Constraints[7] = <<param>>.front_height + 20
  sketch-geometry (10):
    g0: LineSegment StartX=-47 StartY=50 StartZ=0 EndX=47 EndY=50 EndZ=0
    g1: LineSegment StartX=47 StartY=50 StartZ=0 EndX=47 EndY=10.3923 EndZ=0
    g2: LineSegment StartX=36 StartY=-8.66025 StartZ=0 EndX=36 EndY=-34 EndZ=0
    g3: LineSegment StartX=36 StartY=-34 StartZ=0 EndX=-36 EndY=-34 EndZ=0
    g4: LineSegment StartX=-36 StartY=-34 StartZ=0 EndX=-36 EndY=-8.66025 EndZ=0
    g5: LineSegment StartX=-47 StartY=10.3923 StartZ=0 EndX=-47 EndY=50 EndZ=0
    g6: ArcOfCircle CenterX=46 CenterY=-8.66025 CenterZ=0 NormalX=0 NormalY=0 NormalZ=1 AngleXU=0 Radius=10 StartAngle=2.0944 EndAngle=3.14159
    g7: ArcOfCircle CenterX=35 CenterY=10.3923 CenterZ=0 NormalX=0 NormalY=0 NormalZ=1 AngleXU=0 Radius=12 StartAngle=5.23599 EndAngle=6.28319
    g8: ArcOfCircle CenterX=-46 CenterY=-8.66025 CenterZ=0 NormalX=0 NormalY=0 NormalZ=1 AngleXU=0 Radius=10 StartAngle=0 EndAngle=1.0472
    g9: ArcOfCircle CenterX=-35 CenterY=10.3923 CenterZ=0 NormalX=0 NormalY=0 NormalZ=1 AngleXU=0 Radius=12 StartAngle=3.14159 EndAngle=4.18879
  constraints (26):
    c: Vertical(g2)
    c: Vertical(g4)
    c: DistanceX(g4,g2) = 72
    c: Symmetric(g3,g3,g-2)
    c: DistanceY(g3,g-1) = 34
    c: DistanceX(g5,g1) = 94
    c: DistanceX(g5,g1) = 94
    c: DistanceY(g3,g0) = 84
    c: Symmetric(g5,g1,g-2)
    c: Equal(g4,g2)
    c: Coincident(g0,g1)
    c: Coincident(g5,g0)
    c: Symmetric(g0,g0,g-2)
    c: Tangent(g8,g4) = -1.5708
    c: Tangent(g6,g2) = -1.5708
    c: Coincident(g9,g8)
    c: DistanceY(g6,g-1) = 0
    c: Equal(g7,g9)
    c: Radius(g7) = 12
    c: Radius(g6) = 10
    c: Equal(g6,g8)
    c: Tangent(g9,g5) = 1.5708
    c: Tangent(g1,g7) = 1.5708
    c: Tangent(g6,g7) = 1.5708
    c: Coincident(g2,g3)
    c: Coincident(g4,g3)
FEATURE [Sketcher::SketchObject] Sketch031  label="SketchRear"
  ArcFitTolerance = 0
  AttachmentOffset = pos=(0,0,-46) rot=(0,0,1;0rad)
  AttachmentSupport = -> [XZ_Plane006]
  FullyConstrained = true
  MapMode = 5
  Placement = pos=(0,46,1.02e-14) rot=(1,0,0;1.5708rad)
  Support = -> [XZ_Plane006]
  TreeRank = 0
  expr: AttachmentOffset.Base.z = -<<param>>.mid_depth / 2 - <<param>>.back_thickness
  expr: Constraints[10] = <<param>>.front_height + 20
  expr: Constraints[1] = <<param>>.bottom_height + 10
  expr: Constraints[2] = <<param>>.rear_width
  sketch-geometry (4):
    g0: LineSegment StartX=-36 StartY=-34 StartZ=0 EndX=36 EndY=-34 EndZ=0
    g1: LineSegment StartX=36 StartY=50 StartZ=0 EndX=-36 EndY=50 EndZ=0
    g2: LineSegment StartX=36 StartY=-34 StartZ=0 EndX=36 EndY=50 EndZ=0
    g3: LineSegment StartX=-36 StartY=-34 StartZ=0 EndX=-36 EndY=50 EndZ=0
  constraints (12):
    c: Horizontal(g0)
    c: DistanceY(g0,g-1) = 34
    c: DistanceX(g3,g2) = 72
    c: Vertical(g2)
    c: Equal(g3,g2)
    c: Vertical(g3)
    c: Symmetric(g2,g3,g-2)
    c: Coincident(g2,g1)
    c: Coincident(g3,g1)
    c: Equal(g1,g0)
    c: Distance(g2) = 84
    c: Coincident(g2,g0)
FEATURE [Part::Plane] Plane002  label="Plane"
  AttacherType = Attacher::AttachEngine3D
  AttachmentSupport = -> [XZ_Plane006]
  Length = 152
  Placement = pos=(-75,41,-75) rot=(1,0,0;1.5708rad)
  Support = -> [XZ_Plane006]
  TreeRank = 0
  Width = 150
  expr: Placement.Base.y = <<param>>.mid_depth / 2
FEATURE [Sketcher::SketchObject] Sketch032  label="SketchBack"
  ArcFitTolerance = 0
  AttachmentSupport = -> [XZ_Plane]
  FullyConstrained = true
  MapMode = 5
  Placement = pos=(0,0,0) rot=(1,0,0;1.5708rad)
  Support = -> [XZ_Plane]
  TreeRank = 0
  expr: Constraints[10] = <<param>>.rear_screw_width1
  expr: Constraints[11] = <<param>>.reart_screw_width2
  expr: Constraints[12] = <<param>>.rear_screw_height
  expr: Constraints[15] = <<param>>.rear_screw_offset
  expr: Constraints[1] = <<param>>.bottom_height
  expr: Constraints[2] = <<param>>.rear_width
  expr: Constraints[9] = <<param>>.screw_hole + 1
  sketch-geometry (6):
    g0: LineSegment [constr] StartX=36 StartY=-24 StartZ=0 EndX=-36 EndY=-24 EndZ=0
    g1: Circle CenterX=-29 CenterY=8.9 CenterZ=0 NormalX=0 NormalY=0 NormalZ=1 AngleXU=0 Radius=1.75
    g2: Circle CenterX=0 CenterY=8.9 CenterZ=0 NormalX=0 NormalY=0 NormalZ=1 AngleXU=0 Radius=1.75
    g3: Circle CenterX=29 CenterY=8.9 CenterZ=0 NormalX=0 NormalY=0 NormalZ=1 AngleXU=0 Radius=1.75
    g4: Circle CenterX=-27.5 CenterY=-16.6 CenterZ=0 NormalX=0 NormalY=0 NormalZ=1 AngleXU=0 Radius=1.75
    g5: Circle CenterX=27.5 CenterY=-16.6 CenterZ=0 NormalX=0 NormalY=0 NormalZ=1 AngleXU=0 Radius=1.75
  constraints (16):
    c: Symmetric(g0,g0,g-2)
    c: DistanceY(g0,g-1) = 24
    c: DistanceX(g0,g0) = 72
    c: Symmetric(g1,g3,g-2)
    c: Symmetric(g4,g5,g-2)
    c: Equal(g4,g1)
    c: Equal(g1,g2)
    c: Equal(g2,g3)
    c: Equal(g3,g5)
    c: Diameter(g1) = 3.5
    c: DistanceX(g1,g3) = 58
    c: DistanceX(g4,g5) = 55
    c: DistanceY(g5,g3) = 25.5
    c: Horizontal(g1,g2)
    c: PointOnObject(g2,g-2)
    c: DistanceY(g0,g5) = 7.4
FEATURE [Part::Loft] Loft
  Closed = false
  MaxDegree = 5
  Ruled = false
  Sections = -> [Sketch030,Sketch031]
  Solid = true
  TreeRank = 0
FEATURE [Part::Extrusion] Extrude
  Base = -> Sketch012
  Dir = (1,-1e-16,1e-16)
  DirMode = 2
  FaceMakerClass = Part::FaceMakerBullseye
  InnerTaperAngle = 0
  InnerTaperAngleRev = 0
  LengthFwd = 100
  LengthRev = 0
  Solid = true
  Symmetric = true
  TreeRank = 0
FEATURE [Part::MultiCommon] Common
  Shapes = -> [Extrude,Loft]
  TreeRank = 0
FEATURE [Part::FeaturePython] Slice  # WARN: FeaturePython — macro-defined, semantics opaque (R4)
  Base = -> Common
  Mode = 1
  Tolerance = 0
  Tools = -> [Plane002]
  TreeRank = 0
FEATURE [Part::FeaturePython] Slice_child0  label="Slice.Case"  # WARN: FeaturePython — macro-defined, semantics opaque (R4)
  Base = -> Slice
  FilterType = 1
  Invert = false
  OverrideMaxVal = 0
  TreeRank = 0
  WindowFrom = 80
  WindowTo = 100
  items = 0
FEATURE [Part::FeaturePython] Slice_child1  label="Slice.Back"  # WARN: FeaturePython — macro-defined, semantics opaque (R4)
  Base = -> Slice
  FilterType = 1
  Invert = false
  OverrideMaxVal = 0
  TreeRank = 0
  WindowFrom = 80
  WindowTo = 100
  items = 1
FEATURE [App::DocumentObjectGroup] GrExplode_Slice  label="Exploded Slice"
  ClaimAllChildren = true
  ExportMode = 1
  Group = -> [Slice_child0,Slice_child1]
  TreeRank = 0
  _GroupVersion = 1
FEATURE [App::DocumentObjectGroup] Group001  label="BaseShape"
  ClaimAllChildren = true
  ExportMode = 1
  Group = -> [Common,Sketch012,Sketch031,Sketch030,Plane002,GrExplode_Slice]
  TreeRank = 0
  _GroupVersion = 1
FEATURE [PartDesign::FeatureBase] BaseFeature  label="Back.BaseFeature"
  BaseFeature = -> Slice_child1
  NewSolid = false
  Suppress = false
  TreeRank = 0
FEATURE [PartDesign::Pocket] Pocket  label="Back.Pocket.Holes"
  BaseFeature = -> BaseFeature
  ClaimChildren = false
  Fit = 0
  FitJoin = 0
  InnerFit = 0
  InnerFitJoin = 0
  InnerTaperAngle = 0
  InnerTaperAngleRev = 0
  Length = 5
  Length2 = 100
  Midplane = true
  NewSolid = false
  Profile = -> Sketch032
  Suppress = false
  TreeRank = 0
  Type = 1
  _ProfileBasedVersion = 0
FEATURE [PartDesign::Fillet] Fillet  label="Back.Fillet.Big"
  Base = -> Pocket [Edge44,Edge45]
  BaseFeature = -> Pocket
  NewSolid = false
  Radius = 10
  SupportTransform = false
  Suppress = false
  TreeRank = 0
  expr: Radius = <<param>>.radius_big
FEATURE [PartDesign::FeatureBase] BaseFeature001  label="Case.BaseFeature"
  BaseFeature = -> Slice_child0
  NewSolid = false
  Suppress = false
  TreeRank = 0
FEATURE [PartDesign::Pocket] Pocket001  label="Case.Pocket.Batt"
  BaseFeature = -> BaseFeature001
  ClaimChildren = false
  Fit = 0
  FitJoin = 0
  InnerFit = 0
  InnerFitJoin = 0
  InnerTaperAngle = 0
  InnerTaperAngleRev = 0
  Length = 14.6
  Length2 = 100
  NewSolid = false
  Profile = -> Sketch018
  Reversed = true
  Suppress = false
  TreeRank = 0
  Type = 0
  _ProfileBasedVersion = 0
  expr: Length = <<param>>.batt_carveout
FEATURE [PartDesign::Pad] Pad  label="Case.Pad.Batt"
  BaseFeature = -> Pocket001
  ClaimChildren = false
  Direction = (1,1,1)
  Fit = 0
  FitJoin = 0
  InnerFit = 0
  InnerFitJoin = 0
  InnerTaperAngle = 0
  InnerTaperAngleRev = 0
  Length = 45
  Length2 = 100
  NewSolid = false
  Profile = -> Sketch019
  Suppress = false
  TreeRank = 0
  Type = 0
  _ProfileBasedVersion = 0
  expr: Length = <<param>>.batt_rail_length
FEATURE [PartDesign::Pocket] Pocket002  label="Case.Pocket.Support"
  BaseFeature = -> Pad
  ClaimChildren = false
  Fit = 0
  FitJoin = 0
  InnerFit = 0
  InnerFitJoin = 0
  InnerTaperAngle = 0
  InnerTaperAngleRev = 0
  Length = 5
  Length2 = 100
  NewSolid = false
  Profile = -> Sketch
  Suppress = false
  TreeRank = 0
  Type = 0
  _ProfileBasedVersion = 0
FEATURE [PartDesign::Pocket] Pocket006  label="Case.Pocket.Terminal"
  BaseFeature = -> Pocket002
  ClaimChildren = false
  Fit = 0
  FitJoin = 0
  InnerFit = 0
  InnerFitJoin = 0
  InnerTaperAngle = 0
  InnerTaperAngleRev = 0
  Length = 18.5
  Length2 = 100
  NewSolid = false
  Profile = -> Sketch028
  Suppress = false
  TreeRank = 0
  Type = 0
  _ProfileBasedVersion = 0
  expr: Length = <<param>>.mid_depth / 2 - <<param>>.terminal_depth
FEATURE [PartDesign::Pocket] Pocket005  label="Case.Pocket.Access"
  BaseFeature = -> Pocket006
  ClaimChildren = false
  Fit = 0
  FitJoin = 0
  InnerFit = 0
  InnerFitJoin = 0
  InnerTaperAngle = 0
  InnerTaperAngleRev = 0
  Length = 22.5
  Length2 = 100
  NewSolid = false
  Profile = -> Sketch029
  Reversed = true
  Suppress = false
  TreeRank = 0
  Type = 0
  _ProfileBasedVersion = 0
  expr: Length = <<param>>.terminal_depth
FEATURE [Sketcher::SketchObject] Sketch033  label="SketchFace"
  ArcFitTolerance = 0
  AttachmentSupport = -> [XZ_Plane007]
  FullyConstrained = true
  MapMode = 5
  Placement = pos=(0,0,0) rot=(1,0,0;1.5708rad)
  Support = -> [XZ_Plane007]
  TreeRank = 0
  expr: Constraints[12] = <<param>>.face_radius
  expr: Constraints[21] = <<param>>.face_width1 - <<param>>.face_fit
  expr: Constraints[22] = <<param>>.face_width2 - <<param>>.face_fit
  expr: Constraints[23] = <<param>>.face_height - <<param>>.face_fit
  expr: Constraints[27] = <<param>>.screw_hole + 0.8
  expr: Constraints[28] = <<param>>.front_screw_width2 / 2
  expr: Constraints[29] = <<param>>.front_screw_width2 / 2
  expr: Constraints[30] = <<param>>.front_screw_width1 / 2
  expr: Constraints[31] = <<param>>.front_screw_width1 / 2
  expr: Constraints[32] = <<param>>.front_screw_height
  expr: Constraints[35] = <<param>>.front_screw_offset + <<param>>.face_offset - <<param>>.face_fit / 2
  expr: Constraints[48] = <<param>>.face_offset
  expr: Constraints[51] = <<param>>.face_knob_hole / 2
  expr: Constraints[52] = <<param>>.face_knob_x
  expr: Constraints[53] = <<param>>.face_offset + <<param>>.face_knob_y
  expr: Constraints[54] = <<param>>.face_screen_width - 2 * <<param>>.face_screen_radius
  expr: Constraints[55] = <<param>>.face_screen_height - 2 * <<param>>.face_screen_radius
  expr: Constraints[56] = <<param>>.face_offset + <<param>>.face_screen_y - <<param>>.face_screen_height / 2
  expr: Constraints[57] = <<param>>.face_screen_radius
  expr: Constraints[69] = <<param>>.face_plug_hole / 2
  expr: Constraints[71] = <<param>>.face_plug_y + <<param>>.face_offset
  expr: Constraints[72] = <<param>>.face_plug_x
  expr: Constraints[74] = <<param>>.face_screen_x
  sketch-geometry (25):
    g0: LineSegment StartX=-33.8065 StartY=37.4 StartZ=0 EndX=33.8065 EndY=37.4 EndZ=0
    g1: LineSegment StartX=41.8 StartY=29.7224 StartZ=0 EndX=42.55 EndY=11.1223 EndZ=0
    g2: LineSegment StartX=34.5565 StartY=2.8 StartZ=0 EndX=-34.5565 EndY=2.8 EndZ=0
    g3: LineSegment StartX=-42.55 StartY=11.1223 StartZ=0 EndX=-41.8 EndY=29.7224 EndZ=0
    g4: ArcOfCircle CenterX=33.8065 CenterY=29.4 CenterZ=0 NormalX=0 NormalY=0 NormalZ=1 AngleXU=0 Radius=8 StartAngle=0.0403048 EndAngle=1.5708
    g5: ArcOfCircle CenterX=34.5565 CenterY=10.8 CenterZ=0 NormalX=0 NormalY=0 NormalZ=1 AngleXU=0 Radius=8 StartAngle=4.71239 EndAngle=6.32349
    g6: ArcOfCircle CenterX=-33.8065 CenterY=29.4 CenterZ=0 NormalX=0 NormalY=0 NormalZ=1 AngleXU=0 Radius=8 StartAngle=1.5708 EndAngle=3.10129
    g7: ArcOfCircle CenterX=-34.5565 CenterY=10.8 CenterZ=0 NormalX=0 NormalY=0 NormalZ=1 AngleXU=0 Radius=8 StartAngle=3.10129 EndAngle=4.71239
    g8: Circle CenterX=-36.75 CenterY=32.1 CenterZ=0 NormalX=0 NormalY=0 NormalZ=1 AngleXU=0 Radius=1.65
    g9: Circle CenterX=36.75 CenterY=32.1 CenterZ=0 NormalX=0 NormalY=0 NormalZ=1 AngleXU=0 Radius=1.65
    g10: Circle CenterX=-38 CenterY=8.1 CenterZ=0 NormalX=0 NormalY=0 NormalZ=1 AngleXU=0 Radius=1.65
    g11: Circle CenterX=38 CenterY=8.1 CenterZ=0 NormalX=0 NormalY=0 NormalZ=1 AngleXU=0 Radius=1.65
    g12: LineSegment StartX=-11.25 StartY=29.35 StartZ=0 EndX=8.75 EndY=29.35 EndZ=0
    g13: LineSegment StartX=11 StartY=27.1 StartZ=0 EndX=11 EndY=18.5 EndZ=0
    g14: LineSegment StartX=8.75 StartY=16.25 StartZ=0 EndX=-11.25 EndY=16.25 EndZ=0
    g15: LineSegment StartX=-13.5 StartY=18.5 StartZ=0 EndX=-13.5 EndY=27.1 EndZ=0
    g16: ArcOfCircle CenterX=-11.25 CenterY=27.1 CenterZ=0 NormalX=0 NormalY=0 NormalZ=1 AngleXU=0 Radius=2.25 StartAngle=1.5708 EndAngle=3.14159
    g17: ArcOfCircle CenterX=-11.25 CenterY=18.5 CenterZ=0 NormalX=0 NormalY=0 NormalZ=1 AngleXU=0 Radius=2.25 StartAngle=3.14159 EndAngle=4.71239
    g18: ArcOfCircle CenterX=8.75 CenterY=18.5 CenterZ=0 NormalX=0 NormalY=0 NormalZ=1 AngleXU=0 Radius=2.25 StartAngle=4.71239 EndAngle=6.28319
    g19: ArcOfCircle CenterX=8.75 CenterY=27.1 CenterZ=0 NormalX=0 NormalY=0 NormalZ=1 AngleXU=0 Radius=2.25 StartAngle=-9e-16 EndAngle=1.5708
    g20: Circle CenterX=25.5 CenterY=22.3 CenterZ=0 NormalX=0 NormalY=0 NormalZ=1 AngleXU=0 Radius=3.7
    g21: LineSegment StartX=-30.35 StartY=25.9292 StartZ=0 EndX=-25.65 EndY=25.9292 EndZ=0
    g22: LineSegment StartX=-30.35 StartY=14.6708 StartZ=0 EndX=-25.65 EndY=14.6708 EndZ=0
    g23: ArcOfCircle CenterX=-28 CenterY=20.3 CenterZ=0 NormalX=0 NormalY=0 NormalZ=1 AngleXU=0 Radius=6.1 StartAngle=1.96627 EndAngle=4.31691
    g24: ArcOfCircle CenterX=-28 CenterY=20.3 CenterZ=0 NormalX=0 NormalY=0 NormalZ=1 AngleXU=0 Radius=6.1 StartAngle=5.10786 EndAngle=7.45851
  constraints (75):
    c: Coincident(g4,g0)
    c: Coincident(g4,g1)
    c: Coincident(g5,g1)
    c: Coincident(g5,g2)
    c: Coincident(g6,g0)
    c: Coincident(g6,g3)
    c: Coincident(g7,g3)
    c: Coincident(g7,g2)
    c: Equal(g1,g3)
    c: Equal(g4,g6)
    c: Equal(g6,g7)
    c: Equal(g7,g5)
    c: Radius(g4) = 8
    c: Tangent(g6,g3)
    c: Tangent(g7,g3)
    c: Tangent(g7,g2)
    c: Tangent(g6,g0)
    c: Tangent(g4,g0)
    c: Tangent(g4,g1)
    c: Tangent(g5,g1)
    c: Tangent(g5,g2)
    c: DistanceX(g3,g1) = 83.6
    c: DistanceX(g3,g1) = 85.1
    c: DistanceY(g2,g0) = 34.6
    c: Equal(g9,g8)
    c: Equal(g8,g10)
    c: Equal(g10,g11)
    c: Diameter(g8) = 3.3
    c: DistanceX(g10,g-1) = 38
    c: DistanceX(g-1,g11) = 38
    c: DistanceX(g-1,g9) = 36.75
    c: DistanceX(g8,g-1) = 36.75
    c: DistanceY(g11,g9) = 24
    c: Horizontal(g8,g9)
    c: Horizontal(g10,g11)
    c: DistanceY(g-1,g11) = 8.1
    c: Horizontal(g12)
    c: Horizontal(g14)
    c: Vertical(g13)
    c: Vertical(g15)
    c: Tangent(g15,g16) = 1.5708
    c: Tangent(g12,g16) = 1.5708
    c: Tangent(g15,g17) = 1.5708
    c: Tangent(g14,g17) = 1.5708
    c: Tangent(g14,g18) = 1.5708
    c: Tangent(g13,g18) = 1.5708
    c: Tangent(g12,g19) = 1.5708
    c: Tangent(g13,g19) = 1.5708
    c: DistanceY(g-1,g2) = 2.8
    c: Horizontal(g0)
    c: Symmetric(g2,g2,g-2)
    c: Radius(g20) = 3.7
    c: Distance(g20,g-2) = 25.5
    c: Distance(g20,g-1) = 22.3
    c: Distance(g12) = 20
    c: Distance(g15) = 8.6
    c: Distance(g14,g-1) = 16.25
    c: Radius(g19) = 2.25
    c: Equal(g19,g18)
    c: Equal(g18,g17)
    c: Equal(g17,g16)
    c: Horizontal(g21)
    c: Horizontal(g22)
    c: Equal(g21,g22)
    c: Coincident(g23,g21)
    c: Coincident(g23,g22)
    c: Coincident(g24,g23)
    c: Coincident(g24,g21)
    c: Coincident(g24,g22)
    c: Radius(g23) = 6.1
    c: Equal(g24,g23)
    c: Distance(g23,g-1) = 20.3
    c: Distance(g23,g-2) = 28
    c: Distance(g22) = 4.7
    c: Distance(g20,g13) = 14.5
FEATURE [PartDesign::Pad] Pad001  label="OLED.Pad.Face"
  ClaimChildren = false
  Direction = (1,1,1)
  Fit = 0
  FitJoin = 0
  InnerFit = 0
  InnerFitJoin = 0
  InnerTaperAngle = 0
  InnerTaperAngleRev = 0
  Length = 3
  Length2 = 100
  NewSolid = false
  Placement = pos=(0,0,0) rot=(1,0,0;1.5708rad)
  Profile = -> Sketch033
  Suppress = false
  TreeRank = 0
  Type = 0
  _ProfileBasedVersion = 0
  expr: Length = <<param>>.face_thickness
FEATURE [PartDesign::Chamfer] Chamfer001  label="OLED.Chamfer.Screen"
  Angle = 45
  Base = -> Pad001 [Edge34]
  BaseFeature = -> Pad001
  ChamferType = 0
  FlipDirection = false
  NewSolid = false
  Placement = pos=(0,0,0) rot=(1,0,0;1.5708rad)
  Size = 2
  Size2 = 1
  SupportTransform = false
  Suppress = false
  TreeRank = 0
FEATURE [PartDesign::Chamfer] Chamfer002  label="OLED.Chamfer.Screws"
  Angle = 45
  Base = -> Chamfer001 [Edge62,Edge60,Edge61,Edge59]
  BaseFeature = -> Chamfer001
  ChamferType = 0
  FlipDirection = false
  NewSolid = false
  Placement = pos=(0,0,0) rot=(1,0,0;1.5708rad)
  Size = 1.4
  Size2 = 1
  SupportTransform = false
  Suppress = false
  TreeRank = 0
FEATURE [PartDesign::Fillet] Fillet009  label="Back.Fillet.Rear"
  Base = -> Fillet [Edge8]
  BaseFeature = -> Fillet
  NewSolid = false
  Radius = 3
  SupportTransform = false
  Suppress = false
  TreeRank = 0
  expr: Radius = <<param>>.radius_medium
FEATURE [Sketcher::SketchObject] Sketch034  label="SketchKey"
  ArcFitTolerance = 0
  AttachmentOffset = pos=(0,0,-41) rot=(0,0,1;0rad)
  AttachmentSupport = -> [XZ_Plane005]
  FullyConstrained = true
  MapMode = 5
  Placement = pos=(0,41,9.1e-15) rot=(1,0,0;1.5708rad)
  Support = -> [XZ_Plane005]
  TreeRank = 0
  expr: AttachmentOffset.Base.z = -<<param>>.mid_depth / 2
  expr: Constraints[21] = <<param>>.rear_screw_offset
  expr: Constraints[22] = <<param>>.reart_screw_width2
  expr: Constraints[23] = <<param>>.screw_hole / 2
  expr: Constraints[2] = <<param>>.bottom_height
  sketch-geometry (9):
    g0: Circle [constr] CenterX=0 CenterY=-24 CenterZ=0 NormalX=0 NormalY=0 NormalZ=1 AngleXU=0 Radius=3
    g1: LineSegment StartX=4.5 StartY=-24 StartZ=0 EndX=11.5 EndY=-24 EndZ=0
    g2: LineSegment StartX=11.5 StartY=-24 StartZ=0 EndX=11.5 EndY=-22.8 EndZ=0
    g3: LineSegment StartX=4.5 StartY=-24 StartZ=0 EndX=4.5 EndY=-22.8 EndZ=0
    g4: LineSegment StartX=5.5 StartY=-21.8 StartZ=0 EndX=10.5 EndY=-21.8 EndZ=0
    g5: ArcOfCircle CenterX=10.5 CenterY=-22.8 CenterZ=0 NormalX=0 NormalY=0 NormalZ=1 AngleXU=0 Radius=1 StartAngle=1.1e-15 EndAngle=1.5708
    g6: ArcOfCircle CenterX=5.5 CenterY=-22.8 CenterZ=0 NormalX=0 NormalY=0 NormalZ=1 AngleXU=0 Radius=1 StartAngle=1.5708 EndAngle=3.14159
    g7: Circle CenterX=-27.5 CenterY=-16.6 CenterZ=0 NormalX=0 NormalY=0 NormalZ=1 AngleXU=0 Radius=1.25
    g8: Circle CenterX=27.5 CenterY=-16.6 CenterZ=0 NormalX=0 NormalY=0 NormalZ=1 AngleXU=0 Radius=1.25
  constraints (26):
    c: PointOnObject(g0,g-2)
    c: Radius(g0) = 3
    c: DistanceY(g0,g-1) = 24
    c: Horizontal(g1)
    c: Coincident(g2,g1)
    c: Vertical(g2)
    c: Coincident(g3,g1)
    c: Horizontal(g4)
    c: Coincident(g5,g2)
    c: Coincident(g6,g3)
    c: Equal(g5,g6)
    c: Equal(g3,g2)
    c: Tangent(g6,g4) = 1.5708
    c: Tangent(g5,g4) = 1.5708
    c: Vertical(g3)
    c: DistanceX(g1,g1) = 7
    c: DistanceY(g1,g4) = 2.2
    c: DistanceX(g-1,g1) = 4.5
    c: Radius(g6) = 1
    c: Horizontal(g0,g1)
    c: Horizontal(g3,g6)
    c: DistanceY(g0,g7) = 7.4
    c: DistanceX(g7,g8) = 55
    c: Radius(g7) = 1.25
    c: Equal(g7,g8)
    c: Symmetric(g7,g8,g-2)
FEATURE [PartDesign::Pocket] Pocket008  label="Case.Pocket.Key"
  BaseFeature = -> Pocket005
  ClaimChildren = false
  Fit = 0
  FitJoin = 0
  InnerFit = 0
  InnerFitJoin = 0
  InnerTaperAngle = 0
  InnerTaperAngleRev = 0
  Length = 0
  Length2 = 100
  Midplane = true
  NewSolid = false
  Profile = -> Sketch034
  Suppress = false
  TreeRank = 0
  Type = 3
  UpToFace = -> Pocket005 [Face20]
  _ProfileBasedVersion = 0
FEATURE [PartDesign::SubtractiveLoft] SubtractiveLoft  label="Case.SubtractiveLoft"
  BaseFeature = -> Pocket008
  ClaimChildren = false
  Closed = false
  Fit = 0
  FitJoin = 0
  InnerFit = 0
  InnerFitJoin = 0
  NewSolid = false
  Profile = -> Sketch022
  Ruled = true
  Sections = -> [Sketch025,Sketch023]
  Suppress = false
  TreeRank = 0
  _ProfileBasedVersion = 0
FEATURE [PartDesign::Revolution] Revolution  label="Case.Revolution.Button"
  Angle = 360
  Axis = (-3e-16,0.292372,0.956305)
  Base = (-3.1e-15,10,24)
  BaseFeature = -> SubtractiveLoft
  ClaimChildren = false
  Fit = 0
  FitJoin = 0
  InnerFit = 0
  InnerFitJoin = 0
  NewSolid = false
  Profile = -> Sketch021
  ReferenceAxis = -> Sketch021 [V_Axis]
  Reversed = true
  Suppress = false
  TreeRank = 0
  _ProfileBasedVersion = 0
FEATURE [PartDesign::Pocket] Pocket007  label="Case.Pocket.Button"
  BaseFeature = -> Revolution
  ClaimChildren = false
  Fit = 0
  FitJoin = 0
  InnerFit = 0
  InnerFitJoin = 0
  InnerTaperAngle = 0
  InnerTaperAngleRev = 0
  Length = 14
  Length2 = 100
  NewSolid = false
  Profile = -> Sketch008
  Reversed = true
  Suppress = false
  TreeRank = 0
  Type = 0
  _ProfileBasedVersion = 0
FEATURE [PartDesign::Groove] Groove  label="Case.Groove.Button"
  Angle = 360
  Axis = (-3e-16,0.292372,0.956305)
  Base = (-2.7e-15,10,22)
  BaseFeature = -> Pocket007
  ClaimChildren = false
  Fit = 0
  FitJoin = 0
  InnerFit = 0
  InnerFitJoin = 0
  NewSolid = false
  Profile = -> Sketch027
  ReferenceAxis = -> Sketch027 [V_Axis]
  Suppress = false
  TreeRank = 0
  _ProfileBasedVersion = 0
FEATURE [PartDesign::Pocket] Pocket004  label="Case.Pocket.Screws"
  BaseFeature = -> Groove
  ClaimChildren = false
  Fit = 0
  FitJoin = 0
  InnerFit = 0
  InnerFitJoin = 0
  InnerTaperAngle = 0
  InnerTaperAngleRev = 0
  Length = 5
  Length2 = 100
  NewSolid = false
  Profile = -> Sketch026
  Suppress = false
  TreeRank = 0
  Type = 0
  _ProfileBasedVersion = 0
FEATURE [PartDesign::Pocket] Pocket003  label="Case.Pocket.Face"
  BaseFeature = -> Pocket004
  ClaimChildren = false
  Fit = 0
  FitJoin = 0
  InnerFit = 0
  InnerFitJoin = 0
  InnerTaperAngle = 0
  InnerTaperAngleRev = 0
  Length = 4
  Length2 = 100
  NewSolid = false
  Profile = -> Sketch024
  Reversed = true
  Suppress = false
  TreeRank = 0
  Type = 0
  _ProfileBasedVersion = 0
  expr: Length = <<param>>.face_thickness + 1
FEATURE [PartDesign::Fillet] Fillet010  label="Case.Fillet.Button"
  Base = -> Pocket003 [Edge183]
  BaseFeature = -> Pocket003
  NewSolid = false
  Radius = 10
  SupportTransform = false
  Suppress = false
  TreeRank = 0
FEATURE [Mesh::Feature] T12Face
  Placement = pos=(0,-35,20.3) rot=(1,0,0;1.5708rad)
  TreeRank = 1
FEATURE [Sketcher::SketchObject] Sketch035  label="SketchTab"
  ArcFitTolerance = 1e-06
  AttachmentSupport = -> [XZ_Plane007]
  FullyConstrained = true
  MapMode = 5
  Placement = pos=(0,0,0) rot=(1,0,0;1.5708rad)
  Support = -> [XZ_Plane007]
  TreeRank = 8
  expr: Constraints[0] = <<param>>.face_offset + Spreadsheet.face_knob_y + <<param>>.face_knob_tab
  expr: Constraints[2] = <<param>>.face_knob_x
  sketch-geometry (1):
    g0: Circle CenterX=25.5 CenterY=29.3 CenterZ=0 NormalX=0 NormalY=0 NormalZ=1 AngleXU=0 Radius=1.5
  constraints (3):
    c: Distance(g0,g-1) = 29.3
    c: Radius(g0) = 1.5
    c: Distance(g0,g-2) = 25.5
FEATURE [PartDesign::Pocket] Pocket009  label="OLED.Pocket.Tab"
  BaseFeature = -> Chamfer002
  ClaimChildren = false
  Fit = 0
  FitJoin = 0
  InnerFit = 0
  InnerFitJoin = 0
  InnerTaperAngle = 0
  InnerTaperAngleRev = 0
  Length = 1.5
  Length2 = 100
  Linearize = true
  NewSolid = false
  Placement = pos=(0,0,0) rot=(1,0,0;1.5708rad)
  Profile = -> Sketch035
  Reversed = true
  Suppress = false
  TreeRank = 9
  Type = 0
  _ProfileBasedVersion = 1
  expr: Length = <<param>>.face_thickness / 2
FEATURE [PartDesign::Body] Body005  label="BodyOLED"
  AutoGroupSolids = false
  ClaimAllChildren = false
  ExportMode = 0
  Group = -> [Sketch033,Pad001,Chamfer001,Chamfer002,Sketch035,Pocket009]
  Origin = -> Origin007
  Placement = pos=(0,-38,0) rot=(1,0,0;-0.349066rad)
  Tip = -> Pocket009
  TreeRank = 0
  _ExportChildren = -> [Pad001,Chamfer001,Chamfer002,Pocket009]
  _GroupVersion = 1
  expr: Placement.Base.y = -<<param>>.mid_depth / 2 + <<param>>.face_thickness
  expr: Placement.Rotation.Angle = -<<param>>.front_angle
FEATURE [PartDesign::Fillet] Fillet015  label="Back.Fillet.Bottom"
  Base = -> Fillet009 [Edge40,Edge46]
  BaseFeature = -> Fillet009
  NewSolid = false
  Radius = 3
  SupportTransform = false
  Suppress = false
  TreeRank = 22
  expr: Radius = <<param>>.radius_medium
FEATURE [PartDesign::Chamfer] Chamfer  label="Back.Chamfer.Screws"
  Angle = 45
  Base = -> Fillet015 [Edge54,Edge52,Edge50,Edge46,Edge48]
  BaseFeature = -> Fillet015
  ChamferType = 0
  FlipDirection = false
  NewSolid = false
  Size = 1.4
  Size2 = 1
  SupportTransform = false
  Suppress = false
  TreeRank = 0
FEATURE [PartDesign::Body] Body  label="BodyBack"
  AutoGroupSolids = false
  BaseFeature = -> Slice_child1
  ClaimAllChildren = false
  ExportMode = 0
  Group = -> [BaseFeature,Sketch032,Pocket,Fillet,Fillet009,Fillet015,Chamfer]
  Origin = -> Origin
  Tip = -> Chamfer
  TreeRank = 0
  _ExportChildren = -> [BaseFeature,Pocket,Fillet,Fillet009,Fillet015,Chamfer]
  _GroupVersion = 1
FEATURE [PartDesign::Fillet] Fillet016  label="Case.Fillet.Big"
  Base = -> Fillet010 [Edge2,Edge5]
  BaseFeature = -> Fillet010
  NewSolid = false
  Radius = 10
  SupportTransform = false
  Suppress = false
  TreeRank = 23
  expr: Radius = <<param>>.radius_big
FEATURE [PartDesign::Fillet] Fillet017  label="Case.Fillet.Face"
  Base = -> Fillet016 [Edge14,Edge8]
  BaseFeature = -> Fillet016
  NewSolid = false
  Radius = 2
  SupportTransform = false
  Suppress = false
  TreeRank = 24
  expr: Radius = <<param>>.radius_small
FEATURE [PartDesign::Fillet] Fillet018  label="Case.Fillet.Bottom"
  Base = -> Fillet017 [Edge99,Edge96]
  BaseFeature = -> Fillet017
  NewSolid = false
  Radius = 3
  SupportTransform = false
  Suppress = false
  TreeRank = 25
  expr: Radius = <<param>>.radius_medium
FEATURE [PartDesign::Fillet] Fillet019  label="Case.Fillet.lower"
  Base = -> Fillet018 [Edge179]
  BaseFeature = -> Fillet018
  NewSolid = false
  Radius = 2
  SupportTransform = false
  Suppress = false
  TreeRank = 26
  expr: Radius = <<param>>.radius_small
FEATURE [PartDesign::Body] Body004  label="BodyCase"
  AutoGroupSolids = false
  BaseFeature = -> Slice_child0
  ClaimAllChildren = false
  ExportMode = 0
  Group = -> [BaseFeature001,Sketch008,Sketch029,Sketch018,Sketch019,Sketch021,Sketch022,Sketch023,Sketch024,Sketch025,Sketch026,Sketch027,Sketch028,Sketch,Pocket001,Pad,Pocket002,Pocket006,Pocket005,Pocket008,Sketch034,SubtractiveLoft,Revolution,Pocket007,Groove,Pocket004,Pocket003,Fillet010,Fillet016,Fillet017,Fillet018,Fillet019]
  Origin = -> Origin005
  Tip = -> Fillet019
  TreeRank = 0
  _ExportChildren = -> [BaseFeature001,Pocket001,Pad,Pocket002,Pocket006,Pocket005,Pocket008,SubtractiveLoft,Revolution,Pocket007,Groove,Pocket004,Pocket003,Fillet010,Fillet016,Fillet017,Fillet018,Fillet019]
  _GroupVersion = 1
FEATURE [Mesh::Feature] Mesh  label="BodyOLED (Meshed)"
  TreeRank = 27
FEATURE [Mesh::Feature] Mesh001  label="BodyBack (Meshed)"
  TreeRank = 28
FEATURE [Mesh::Feature] Mesh002  label="BodyCase (Meshed)"
  TreeRank = 29
FEATURE [App::DocumentObjectGroup] Group002  label="Mesh"
  ClaimAllChildren = true
  ExportMode = 1
  Group = -> [T12Face,Mesh,Mesh001,Mesh002]
  TreeRank = 0
  _GroupVersion = 1
FEATURE [App::Part] Part
  ClaimAllChildren = false
  ExportMode = 1
  Group = -> [Extrude,Plane002,Common,Sketch012,Loft,Slice_child1,Slice_child0,Slice,GrExplode_Slice,Sketch030,Sketch031,Group001,Spreadsheet,Body,Body004,Body005,Group002,T12Face,Mesh,Mesh001,Mesh002]
  Origin = -> Origin006
  TreeRank = 0
  _ExportChildren = -> [Group001,Spreadsheet,Body,Body004,Body005,Group002]
  _GroupVersion = 1
